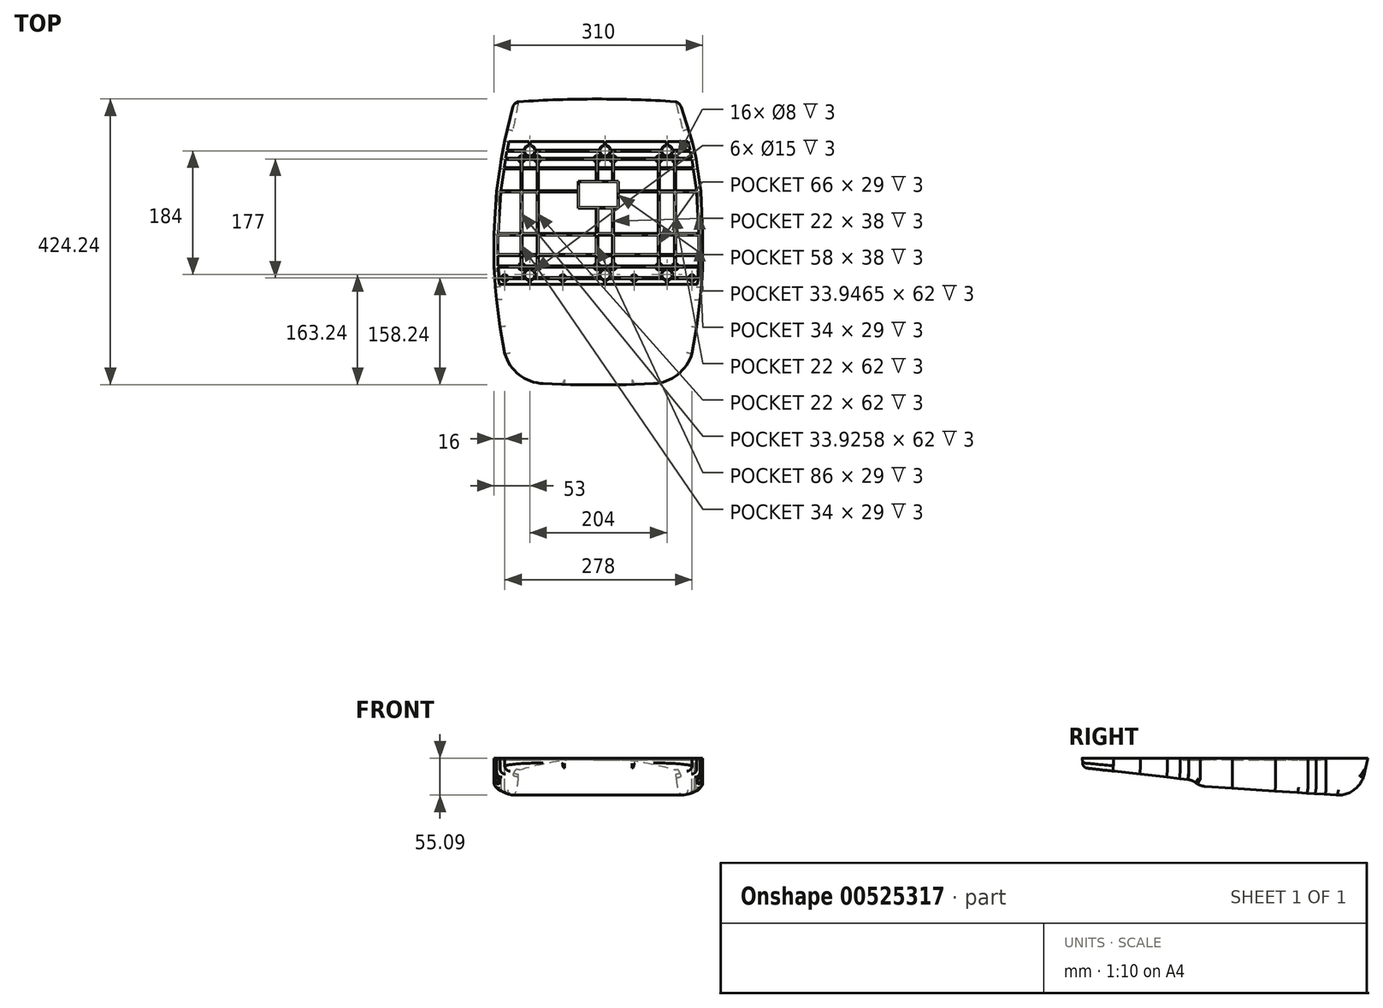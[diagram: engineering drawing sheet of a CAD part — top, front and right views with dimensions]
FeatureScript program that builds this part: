
annotation { "Feature Type Name" : "Feature", "Feature Type Description" : "" }
export const myFeature = defineFeature(function(context is Context, id is Id, definition is map)
    precondition{}
    {
        {
            var Q0;
            Q0=qCreatedBy(makeId("Top.planeOp"),FACE);
            var sketch = newSketch(context, id + "F0", { "sketchPlane" : qUnion([Q0])});
            skLineSegment(sketch, "E0.bottom", {"start": v(29, 19) * mm, "end": v(-29, 19) * mm});
            skLineSegment(sketch, "E0.top", {"start": v(29, -19) * mm, "end": v(-29, -19) * mm});
            skLineSegment(sketch, "E0.left", {"start": v(29, 19) * mm, "end": v(29, -19) * mm});
            skLineSegment(sketch, "E0.right", {"start": v(-29, 19) * mm, "end": v(-29, -19) * mm});
            skPoint(sketch, "E0.middle", {"position": v(0, 0) * mm});
            skLineSegment(sketch, "E1.0", {"start": v(30, 20) * mm, "end": v(-30, 20) * mm});
            skLineSegment(sketch, "E1.1", {"start": v(30, 20) * mm, "end": v(30, -20) * mm});
            skLineSegment(sketch, "E1.2", {"start": v(30, -20) * mm, "end": v(-30, -20) * mm});
            skLineSegment(sketch, "E1.3", {"start": v(-30, 20) * mm, "end": v(-30, -20) * mm});
            skLineSegment(sketch, "E2", {"start": v(-2, 53) * mm, "end": v(-2, -107) * mm, "construction": true});
            skLineSegment(sketch, "E3", {"start": v(22, 53) * mm, "end": v(22, -107) * mm, "construction": true});
            skLineSegment(sketch, "E4", {"start": v(-155, -107) * mm, "end": v(155, -107) * mm, "construction": true});
            skLineSegment(sketch, "E5", {"start": v(155, -90) * mm, "end": v(-155, -90) * mm, "construction": true});
            skLineSegment(sketch, "E6", {"start": v(-155, -59) * mm, "end": v(155, -59) * mm, "construction": true});
            skCircle(sketch, "E7", {"center": v(-2, -107) * mm, "radius": 5 * mm});
            skCircle(sketch, "E8", {"center": v(22, -107) * mm, "radius": 5 * mm});
            skLineSegment(sketch, "E9", {"start": v(154, -124) * mm, "end": v(-154, -124) * mm, "construction": true});
            skCircle(sketch, "E10", {"center": v(139, -124) * mm, "radius": 5 * mm});
            skCircle(sketch, "E11", {"center": v(53, -124) * mm, "radius": 5 * mm});
            skCircle(sketch, "E12", {"center": v(-53, -124) * mm, "radius": 5 * mm});
            skCircle(sketch, "E13", {"center": v(-139, -124) * mm, "radius": 5 * mm});
            skLineSegment(sketch, "E14", {"start": v(22, -107) * mm, "end": v(10, -119) * mm, "construction": true});
            skLineSegment(sketch, "E15", {"start": v(-2, -107) * mm, "end": v(10, -119) * mm, "construction": true});
            skCircle(sketch, "E16", {"center": v(10, -119) * mm, "radius": 8.5 * mm});
            skCircle(sketch, "E17", {"center": v(90, -107) * mm, "radius": 5 * mm});
            skCircle(sketch, "E18", {"center": v(114, -107) * mm, "radius": 5 * mm});
            skLineSegment(sketch, "E19", {"start": v(114, -107) * mm, "end": v(102, -119) * mm, "construction": true});
            skLineSegment(sketch, "E20", {"start": v(102, -119) * mm, "end": v(90, -107) * mm, "construction": true});
            skCircle(sketch, "E21", {"center": v(102, -119) * mm, "radius": 8.5 * mm});
            skCircle(sketch, "E22", {"center": v(-90, -107) * mm, "radius": 5 * mm});
            skCircle(sketch, "E23", {"center": v(-114, -107) * mm, "radius": 5 * mm});
            skLineSegment(sketch, "E24", {"start": v(-90, -107) * mm, "end": v(-102, -119) * mm, "construction": true});
            skLineSegment(sketch, "E25", {"start": v(-102, -119) * mm, "end": v(-114, -107) * mm, "construction": true});
            skCircle(sketch, "E26", {"center": v(-102, -119) * mm, "radius": 8.5 * mm});
            skLineSegment(sketch, "E27", {"start": v(-90, -107) * mm, "end": v(-90, 53) * mm, "construction": true});
            skLineSegment(sketch, "E28", {"start": v(-114, -107) * mm, "end": v(-114, 53) * mm, "construction": true});
            skLineSegment(sketch, "E29", {"start": v(114, -107) * mm, "end": v(114, 53) * mm, "construction": true});
            skLineSegment(sketch, "E30", {"start": v(145, 53) * mm, "end": v(-144, 53) * mm, "construction": true});
            skLineSegment(sketch, "E31", {"start": v(90, -107) * mm, "end": v(90, 53) * mm, "construction": true});
            skLineSegment(sketch, "E32", {"start": v(152, 5) * mm, "end": v(-151, 5) * mm, "construction": true});
            skLineSegment(sketch, "E33", {"start": v(142.5, 65) * mm, "end": v(-135.68, 65) * mm, "construction": true});
            skLineSegment(sketch, "E34", {"start": v(-146, 39) * mm, "end": v(147, 39) * mm, "construction": true});
            skCircle(sketch, "E35", {"center": v(-114, 53) * mm, "radius": 5 * mm});
            skCircle(sketch, "E36", {"center": v(-90, 53) * mm, "radius": 5 * mm});
            skCircle(sketch, "E37", {"center": v(-2, 53) * mm, "radius": 5 * mm});
            skCircle(sketch, "E38", {"center": v(22, 53) * mm, "radius": 5 * mm});
            skCircle(sketch, "E39", {"center": v(90, 53) * mm, "radius": 5 * mm});
            skCircle(sketch, "E40", {"center": v(114, 53) * mm, "radius": 5 * mm});
            skLineSegment(sketch, "E41", {"start": v(-114, 53) * mm, "end": v(-102, 65) * mm, "construction": true});
            skLineSegment(sketch, "E42", {"start": v(-102, 65) * mm, "end": v(-90, 53) * mm, "construction": true});
            skLineSegment(sketch, "E43", {"start": v(-2, 53) * mm, "end": v(10, 65) * mm, "construction": true});
            skLineSegment(sketch, "E44", {"start": v(10, 65) * mm, "end": v(22, 53) * mm, "construction": true});
            skLineSegment(sketch, "E45", {"start": v(90, 53) * mm, "end": v(102, 65) * mm, "construction": true});
            skLineSegment(sketch, "E46", {"start": v(102, 65) * mm, "end": v(114, 53) * mm, "construction": true});
            skCircle(sketch, "E47", {"center": v(102, 65) * mm, "radius": 8.5 * mm});
            skCircle(sketch, "E48", {"center": v(10, 65) * mm, "radius": 8.5 * mm});
            skCircle(sketch, "E49", {"center": v(-102, 65) * mm, "radius": 8.5 * mm});
            skLineSegment(sketch, "E50", {"start": v(-53, -133) * mm, "end": v(-53, -107) * mm, "construction": true});
            skLineSegment(sketch, "E51", {"start": v(10, -119) * mm, "end": v(10, -133) * mm, "construction": true});
            skLineSegment(sketch, "E52", {"start": v(53, -133) * mm, "end": v(53, -107) * mm, "construction": true});
            skLineSegment(sketch, "E53", {"start": v(139, -133) * mm, "end": v(139, -107) * mm, "construction": true});
            skLineSegment(sketch, "E54", {"start": v(102, -119) * mm, "end": v(102, -137) * mm, "construction": true});
            skLineSegment(sketch, "E55", {"start": v(-139, -133) * mm, "end": v(-139, -107) * mm, "construction": true});
            skLineSegment(sketch, "E56", {"start": v(-102, -119) * mm, "end": v(-102, -137) * mm, "construction": true});
            skLineSegment(sketch, "E57", {"start": v(-102, 65) * mm, "end": v(-102, 80) * mm, "construction": true});
            skLineSegment(sketch, "E58", {"start": v(10, 65) * mm, "end": v(10, 80) * mm, "construction": true});
            skLineSegment(sketch, "E59", {"start": v(102, 65) * mm, "end": v(102, 80) * mm, "construction": true});
            skLineSegment(sketch, "E60", {"start": v(23, -20) * mm, "end": v(23, -58) * mm});
            skLineSegment(sketch, "E61", {"start": v(23, -58) * mm, "end": v(89, -58) * mm});
            skLineSegment(sketch, "E62", {"start": v(89, -58) * mm, "end": v(89, 4) * mm});
            skLineSegment(sketch, "E63", {"start": v(89, 4) * mm, "end": v(30, 4) * mm});
            skLineSegment(sketch, "E64", {"start": v(21, -20) * mm, "end": v(21, -58) * mm});
            skLineSegment(sketch, "E65", {"start": v(21, -58) * mm, "end": v(-1, -58) * mm});
            skLineSegment(sketch, "E66", {"start": v(-1, -58) * mm, "end": v(-1, -20) * mm});
            skLineSegment(sketch, "E67", {"start": v(-3, -20) * mm, "end": v(-3, -58) * mm});
            skLineSegment(sketch, "E68", {"start": v(-3, -58) * mm, "end": v(-89, -58) * mm});
            skLineSegment(sketch, "E69", {"start": v(-89, -58) * mm, "end": v(-89, 4) * mm});
            skLineSegment(sketch, "E70", {"start": v(-89, 4) * mm, "end": v(-30, 4) * mm});
            skLineSegment(sketch, "E71", {"start": v(21, -60) * mm, "end": v(21, -89) * mm});
            skLineSegment(sketch, "E72", {"start": v(21, -89) * mm, "end": v(-1, -89) * mm});
            skLineSegment(sketch, "E73", {"start": v(-1, -89) * mm, "end": v(-1, -60) * mm});
            skLineSegment(sketch, "E74", {"start": v(-1, -60) * mm, "end": v(21, -60) * mm});
            skLineSegment(sketch, "E75", {"start": v(23, -60) * mm, "end": v(23, -89) * mm});
            skLineSegment(sketch, "E76", {"start": v(23, -89) * mm, "end": v(89, -89) * mm});
            skLineSegment(sketch, "E77", {"start": v(89, -89) * mm, "end": v(89, -60) * mm});
            skLineSegment(sketch, "E78", {"start": v(89, -60) * mm, "end": v(23, -60) * mm});
            skLineSegment(sketch, "E79", {"start": v(-3, -60) * mm, "end": v(-89, -60) * mm});
            skLineSegment(sketch, "E80", {"start": v(-89, -60) * mm, "end": v(-89, -89) * mm});
            skLineSegment(sketch, "E81", {"start": v(-89, -89) * mm, "end": v(-3, -89) * mm});
            skLineSegment(sketch, "E82", {"start": v(-3, -89) * mm, "end": v(-3, -60) * mm});
            skLineSegment(sketch, "E83", {"start": v(21, -91) * mm, "end": v(21, -102.1) * mm});
            skLineSegment(sketch, "E84", {"start": v(21, -91) * mm, "end": v(-1, -91) * mm});
            skLineSegment(sketch, "E85", {"start": v(-1, -91) * mm, "end": v(-1, -102.1) * mm});
            skLineSegment(sketch, "E86", {"start": v(2.9, -106) * mm, "end": v(17.1, -106) * mm});
            skLineSegment(sketch, "E87", {"start": v(17.83, -109.76) * mm, "end": v(15.26, -112.32) * mm});
            skLineSegment(sketch, "E88", {"start": v(4.74, -112.32) * mm, "end": v(2.17, -109.76) * mm});
            skLineSegment(sketch, "E89", {"start": v(2.9, -108) * mm, "end": v(17.1, -108) * mm});
            skLineSegment(sketch, "E90", {"start": v(19.24, -111.17) * mm, "end": v(16.68, -113.74) * mm});
            skLineSegment(sketch, "E91", {"start": v(0.76, -111.17) * mm, "end": v(3.32, -113.74) * mm});
            skCircle(sketch, "E92", {"center": v(10, -119) * mm, "radius": 7.5 * mm});
            skCircle(sketch, "E93", {"center": v(-2, -107) * mm, "radius": 4 * mm});
            skCircle(sketch, "E94", {"center": v(22, -107) * mm, "radius": 4 * mm});
            skCircle(sketch, "E95", {"center": v(53, -124) * mm, "radius": 4 * mm});
            skCircle(sketch, "E96", {"center": v(90, -107) * mm, "radius": 4 * mm});
            skCircle(sketch, "E97", {"center": v(114, -107) * mm, "radius": 4 * mm});
            skCircle(sketch, "E98", {"center": v(139, -124) * mm, "radius": 4 * mm});
            skCircle(sketch, "E99", {"center": v(-53, -124) * mm, "radius": 4 * mm});
            skCircle(sketch, "E100", {"center": v(-90, -107) * mm, "radius": 4 * mm});
            skCircle(sketch, "E101", {"center": v(-139, -124) * mm, "radius": 4 * mm});
            skCircle(sketch, "E102", {"center": v(-114, -107) * mm, "radius": 4 * mm});
            skCircle(sketch, "E103", {"center": v(-114, 53) * mm, "radius": 4 * mm});
            skCircle(sketch, "E104", {"center": v(-90, 53) * mm, "radius": 4 * mm});
            skCircle(sketch, "E105", {"center": v(-2, 53) * mm, "radius": 4 * mm});
            skCircle(sketch, "E106", {"center": v(114, 53) * mm, "radius": 4 * mm});
            skCircle(sketch, "E107", {"center": v(22, 53) * mm, "radius": 4 * mm});
            skCircle(sketch, "E108", {"center": v(90, 53) * mm, "radius": 4 * mm});
            skCircle(sketch, "E109", {"center": v(102, -119) * mm, "radius": 7.5 * mm});
            skCircle(sketch, "E110", {"center": v(-102, -119) * mm, "radius": 7.5 * mm});
            skCircle(sketch, "E111", {"center": v(-102, 65) * mm, "radius": 7.5 * mm});
            skCircle(sketch, "E112", {"center": v(10, 65) * mm, "radius": 7.5 * mm});
            skCircle(sketch, "E113", {"center": v(102, 65) * mm, "radius": 7.5 * mm});
            skLineSegment(sketch, "E114", {"start": v(17.5, -123) * mm, "end": v(48.1, -123) * mm});
            skLineSegment(sketch, "E115", {"start": v(48.1, -125) * mm, "end": v(16.02, -125) * mm});
            skLineSegment(sketch, "E116", {"start": v(26.9, -106) * mm, "end": v(85.1, -106) * mm});
            skLineSegment(sketch, "E117", {"start": v(23, -91) * mm, "end": v(23, -102.1) * mm});
            skLineSegment(sketch, "E118", {"start": v(23, -91) * mm, "end": v(89, -91) * mm});
            skLineSegment(sketch, "E119", {"start": v(89, -91) * mm, "end": v(89, -102.1) * mm});
            skLineSegment(sketch, "E120", {"start": v(26.9, -108) * mm, "end": v(85.1, -108) * mm});
            skLineSegment(sketch, "E121", {"start": v(57.9, -123) * mm, "end": v(94.5, -123) * mm});
            skLineSegment(sketch, "E122", {"start": v(95.32, -113.74) * mm, "end": v(92.76, -111.17) * mm});
            skLineSegment(sketch, "E123", {"start": v(96.74, -112.32) * mm, "end": v(94.17, -109.76) * mm});
            skLineSegment(sketch, "E124", {"start": v(94.9, -108) * mm, "end": v(109.1, -108) * mm});
            skLineSegment(sketch, "E125", {"start": v(107.26, -112.32) * mm, "end": v(109.83, -109.76) * mm});
            skLineSegment(sketch, "E126", {"start": v(108.68, -113.74) * mm, "end": v(111.24, -111.17) * mm});
            skLineSegment(sketch, "E127", {"start": v(109.5, -123) * mm, "end": v(134.1, -123) * mm});
            skLineSegment(sketch, "E128", {"start": v(118.9, -108) * mm, "end": v(148.93, -108) * mm});
            skLineSegment(sketch, "E129", {"start": v(91, -58) * mm, "end": v(113, -58) * mm});
            skLineSegment(sketch, "E130", {"start": v(113, -58) * mm, "end": v(113, 4) * mm});
            skLineSegment(sketch, "E131", {"start": v(113, 4) * mm, "end": v(91, 4) * mm});
            skLineSegment(sketch, "E132", {"start": v(91, 4) * mm, "end": v(91, -58) * mm});
            skLineSegment(sketch, "E133", {"start": v(91, -60) * mm, "end": v(91, -89) * mm});
            skLineSegment(sketch, "E134", {"start": v(91, -89) * mm, "end": v(113, -89) * mm});
            skLineSegment(sketch, "E135", {"start": v(113, -89) * mm, "end": v(113, -60) * mm});
            skLineSegment(sketch, "E136", {"start": v(113, -60) * mm, "end": v(91, -60) * mm});
            skLineSegment(sketch, "E137", {"start": v(91, -91) * mm, "end": v(91, -102.1) * mm});
            skLineSegment(sketch, "E138", {"start": v(91, -91) * mm, "end": v(113, -91) * mm});
            skLineSegment(sketch, "E139", {"start": v(113, -91) * mm, "end": v(113, -102.1) * mm});
            skLineSegment(sketch, "E140", {"start": v(89, 6) * mm, "end": v(30, 6) * mm});
            skLineSegment(sketch, "E141", {"start": v(89, 6) * mm, "end": v(89, 38) * mm});
            skLineSegment(sketch, "E142", {"start": v(89, 38) * mm, "end": v(23, 38) * mm});
            skLineSegment(sketch, "E143", {"start": v(23, 38) * mm, "end": v(23, 20) * mm});
            skLineSegment(sketch, "E144", {"start": v(91, 6) * mm, "end": v(113, 6) * mm});
            skLineSegment(sketch, "E145", {"start": v(113, 6) * mm, "end": v(113, 38) * mm});
            skLineSegment(sketch, "E146", {"start": v(113, 38) * mm, "end": v(91, 38) * mm});
            skLineSegment(sketch, "E147", {"start": v(91, 38) * mm, "end": v(91, 6) * mm});
            skLineSegment(sketch, "E148", {"start": v(113, 40) * mm, "end": v(113, 48.1) * mm});
            skLineSegment(sketch, "E149", {"start": v(113, 40) * mm, "end": v(91, 40) * mm});
            skLineSegment(sketch, "E150", {"start": v(91, 40) * mm, "end": v(91, 48.1) * mm});
            skLineSegment(sketch, "E151", {"start": v(94.9, 52) * mm, "end": v(109.1, 52) * mm});
            skLineSegment(sketch, "E152", {"start": v(89, 40) * mm, "end": v(89, 48.1) * mm});
            skLineSegment(sketch, "E153", {"start": v(89, 40) * mm, "end": v(23, 40) * mm});
            skLineSegment(sketch, "E154", {"start": v(23, 40) * mm, "end": v(23, 48.1) * mm});
            skLineSegment(sketch, "E155", {"start": v(85.1, 52) * mm, "end": v(26.9, 52) * mm});
            skLineSegment(sketch, "E156", {"start": v(21, 20) * mm, "end": v(21, 38) * mm});
            skLineSegment(sketch, "E157", {"start": v(21, 38) * mm, "end": v(-1, 38) * mm});
            skLineSegment(sketch, "E158", {"start": v(-1, 38) * mm, "end": v(-1, 20) * mm});
            skLineSegment(sketch, "E159", {"start": v(21, 40) * mm, "end": v(-1, 40) * mm});
            skLineSegment(sketch, "E160", {"start": v(-1, 40) * mm, "end": v(-1, 48.1) * mm});
            skLineSegment(sketch, "E161", {"start": v(17.1, 52) * mm, "end": v(2.9, 52) * mm});
            skLineSegment(sketch, "E162", {"start": v(21, 40) * mm, "end": v(21, 48.1) * mm});
            skLineSegment(sketch, "E163", {"start": v(-3, -91) * mm, "end": v(-89, -91) * mm});
            skLineSegment(sketch, "E164", {"start": v(-89, -91) * mm, "end": v(-89, -102.1) * mm});
            skLineSegment(sketch, "E165", {"start": v(-3, -91) * mm, "end": v(-3, -102.1) * mm});
            skLineSegment(sketch, "E166", {"start": v(-6.9, -106) * mm, "end": v(-85.1, -106) * mm});
            skLineSegment(sketch, "E167", {"start": v(-94.9, -106) * mm, "end": v(-109.1, -106) * mm});
            skLineSegment(sketch, "E168", {"start": v(-91, -58) * mm, "end": v(-113, -58) * mm});
            skLineSegment(sketch, "E169", {"start": v(-113, -58) * mm, "end": v(-113, 4) * mm});
            skLineSegment(sketch, "E170", {"start": v(-113, 4) * mm, "end": v(-91, 4) * mm});
            skLineSegment(sketch, "E171", {"start": v(-91, 4) * mm, "end": v(-91, -58) * mm});
            skLineSegment(sketch, "E172", {"start": v(-30, 6) * mm, "end": v(-89, 6) * mm});
            skLineSegment(sketch, "E173", {"start": v(-89, 6) * mm, "end": v(-89, 38) * mm});
            skLineSegment(sketch, "E174", {"start": v(-89, 38) * mm, "end": v(-3, 38) * mm});
            skLineSegment(sketch, "E175", {"start": v(-3, 38) * mm, "end": v(-3, 20) * mm});
            skLineSegment(sketch, "E176", {"start": v(-91, 6) * mm, "end": v(-113, 6) * mm});
            skLineSegment(sketch, "E177", {"start": v(-113, 6) * mm, "end": v(-113, 38) * mm});
            skLineSegment(sketch, "E178", {"start": v(-113, 38) * mm, "end": v(-91, 38) * mm});
            skLineSegment(sketch, "E179", {"start": v(-91, 38) * mm, "end": v(-91, 6) * mm});
            skLineSegment(sketch, "E180", {"start": v(-3, 40) * mm, "end": v(-89, 40) * mm});
            skLineSegment(sketch, "E181", {"start": v(-89, 40) * mm, "end": v(-89, 48.1) * mm});
            skLineSegment(sketch, "E182", {"start": v(-3, 40) * mm, "end": v(-3, 48.1) * mm});
            skLineSegment(sketch, "E183", {"start": v(-6.9, 52) * mm, "end": v(-85.1, 52) * mm});
            skLineSegment(sketch, "E184", {"start": v(-91, 40) * mm, "end": v(-113, 40) * mm});
            skLineSegment(sketch, "E185", {"start": v(-113, 40) * mm, "end": v(-113, 48.1) * mm});
            skLineSegment(sketch, "E186", {"start": v(-91, 40) * mm, "end": v(-91, 48.1) * mm});
            skLineSegment(sketch, "E187", {"start": v(-94.9, 52) * mm, "end": v(-109.1, 52) * mm});
            skLineSegment(sketch, "E188", {"start": v(57.9, -125) * mm, "end": v(95.98, -125) * mm});
            skLineSegment(sketch, "E189", {"start": v(108.02, -125) * mm, "end": v(134.1, -125) * mm});
            skLineSegment(sketch, "E190", {"start": v(3.98, -125) * mm, "end": v(-48.1, -125) * mm});
            skLineSegment(sketch, "E191", {"start": v(2.5, -123) * mm, "end": v(-48.1, -123) * mm});
            skLineSegment(sketch, "E192", {"start": v(-57.9, -125) * mm, "end": v(-95.98, -125) * mm});
            skLineSegment(sketch, "E193", {"start": v(-57.9, -123) * mm, "end": v(-94.5, -123) * mm});
            skLineSegment(sketch, "E194", {"start": v(-95.32, -113.74) * mm, "end": v(-92.76, -111.17) * mm});
            skLineSegment(sketch, "E195", {"start": v(-96.74, -112.32) * mm, "end": v(-94.17, -109.76) * mm});
            skLineSegment(sketch, "E196", {"start": v(-6.9, -108) * mm, "end": v(-85.1, -108) * mm});
            skLineSegment(sketch, "E197", {"start": v(-108.02, -125) * mm, "end": v(-134.1, -125) * mm});
            skLineSegment(sketch, "E198", {"start": v(-109.5, -123) * mm, "end": v(-134.1, -123) * mm});
            skLineSegment(sketch, "E199", {"start": v(-94.9, -108) * mm, "end": v(-109.1, -108) * mm});
            skLineSegment(sketch, "E200", {"start": v(-107.26, -112.32) * mm, "end": v(-109.83, -109.76) * mm});
            skLineSegment(sketch, "E201", {"start": v(-108.68, -113.74) * mm, "end": v(-111.24, -111.17) * mm});
            skLineSegment(sketch, "E202", {"start": v(2.9, 54) * mm, "end": v(17.1, 54) * mm});
            skLineSegment(sketch, "E203", {"start": v(26.9, 54) * mm, "end": v(85.1, 54) * mm});
            skLineSegment(sketch, "E204", {"start": v(94.9, 54) * mm, "end": v(109.1, 54) * mm});
            skLineSegment(sketch, "E205", {"start": v(109.83, 55.76) * mm, "end": v(107.26, 58.32) * mm});
            skLineSegment(sketch, "E206", {"start": v(111.24, 57.17) * mm, "end": v(108.68, 59.74) * mm});
            skLineSegment(sketch, "E207", {"start": v(96.74, 58.32) * mm, "end": v(94.17, 55.76) * mm});
            skLineSegment(sketch, "E208", {"start": v(92.76, 57.17) * mm, "end": v(95.32, 59.74) * mm});
            skLineSegment(sketch, "E209", {"start": v(93.56, 64) * mm, "end": v(18.44, 64) * mm});
            skLineSegment(sketch, "E210", {"start": v(93.56, 66) * mm, "end": v(18.44, 66) * mm});
            skLineSegment(sketch, "E211", {"start": v(19.24, 57.17) * mm, "end": v(16.68, 59.74) * mm});
            skLineSegment(sketch, "E212", {"start": v(17.83, 55.76) * mm, "end": v(15.26, 58.32) * mm});
            skLineSegment(sketch, "E213", {"start": v(2.17, 55.76) * mm, "end": v(4.74, 58.32) * mm});
            skLineSegment(sketch, "E214", {"start": v(0.76, 57.17) * mm, "end": v(3.32, 59.74) * mm});
            skLineSegment(sketch, "E215", {"start": v(-6.9, 54) * mm, "end": v(-85.1, 54) * mm});
            skLineSegment(sketch, "E216", {"start": v(-94.9, 54) * mm, "end": v(-109.1, 54) * mm});
            skLineSegment(sketch, "E217", {"start": v(-109.83, 55.76) * mm, "end": v(-107.26, 58.32) * mm});
            skLineSegment(sketch, "E218", {"start": v(-111.24, 57.17) * mm, "end": v(-108.68, 59.74) * mm});
            skLineSegment(sketch, "E219", {"start": v(-94.17, 55.76) * mm, "end": v(-96.74, 58.32) * mm});
            skLineSegment(sketch, "E220", {"start": v(-92.76, 57.17) * mm, "end": v(-95.32, 59.74) * mm});
            skLineSegment(sketch, "E221", {"start": v(1.56, 64) * mm, "end": v(-93.56, 64) * mm});
            skLineSegment(sketch, "E222", {"start": v(1.56, 66) * mm, "end": v(-93.56, 66) * mm});
            skLineSegment(sketch, "E223", {"start": v(-91, -60) * mm, "end": v(-113, -60) * mm});
            skLineSegment(sketch, "E224", {"start": v(-113, -60) * mm, "end": v(-113, -89) * mm});
            skLineSegment(sketch, "E225", {"start": v(-113, -89) * mm, "end": v(-91, -89) * mm});
            skLineSegment(sketch, "E226", {"start": v(-91, -89) * mm, "end": v(-91, -60) * mm});
            skLineSegment(sketch, "E227", {"start": v(-91, -91) * mm, "end": v(-113, -91) * mm});
            skLineSegment(sketch, "E228", {"start": v(-113, -91) * mm, "end": v(-113, -102.1) * mm});
            skLineSegment(sketch, "E229", {"start": v(-91, -91) * mm, "end": v(-91, -102.1) * mm});
            skLineSegment(sketch, "E230", {"start": v(-144, 53) * mm, "end": v(-146, 39) * mm});
            skLineSegment(sketch, "E231", {"start": v(-146, 39) * mm, "end": v(-151, 5) * mm});
            skLineSegment(sketch, "E232", {"start": v(-151, 5) * mm, "end": v(-155, -59) * mm});
            skLineSegment(sketch, "E233", {"start": v(-155, -59) * mm, "end": v(-155, -90) * mm});
            skLineSegment(sketch, "E234", {"start": v(-155, -90) * mm, "end": v(-155, -107) * mm});
            skLineSegment(sketch, "E235", {"start": v(-155, -107) * mm, "end": v(-154, -124) * mm});
            skLineSegment(sketch, "E236", {"start": v(142.5, 65) * mm, "end": v(145, 53) * mm});
            skLineSegment(sketch, "E237", {"start": v(145, 53) * mm, "end": v(147, 39) * mm});
            skLineSegment(sketch, "E238", {"start": v(147, 39) * mm, "end": v(152, 5) * mm});
            skLineSegment(sketch, "E239", {"start": v(152, 5) * mm, "end": v(155, -59) * mm});
            skLineSegment(sketch, "E240", {"start": v(155, -59) * mm, "end": v(155, -90) * mm});
            skLineSegment(sketch, "E241", {"start": v(155, -90) * mm, "end": v(155, -107) * mm});
            skLineSegment(sketch, "E242", {"start": v(155, -107) * mm, "end": v(154, -124) * mm});
            skLineSegment(sketch, "E243", {"start": v(139, 80) * mm, "end": v(-139, 80) * mm, "construction": true});
            skLineSegment(sketch, "E244", {"start": v(-139, 80) * mm, "end": v(-144, 53) * mm});
            skLineSegment(sketch, "E245", {"start": v(139, 80) * mm, "end": v(142.5, 65) * mm});
            skLineSegment(sketch, "E246", {"start": v(-153.3, -133) * mm, "end": v(153.3, -133) * mm, "construction": true});
            skLineSegment(sketch, "E247", {"start": v(-154, -124) * mm, "end": v(-153.3, -133) * mm});
            skLineSegment(sketch, "E248", {"start": v(154, -124) * mm, "end": v(153.3, -133) * mm});
            skLineSegment(sketch, "E249.0", {"start": v(148.01, -123.6) * mm, "end": v(147.29, -133) * mm});
            skLineSegment(sketch, "E249.1", {"start": v(149, -106.82) * mm, "end": v(148.01, -123.6) * mm});
            skLineSegment(sketch, "E249.2", {"start": v(149, -90) * mm, "end": v(149, -106.82) * mm});
            skLineSegment(sketch, "E249.3", {"start": v(149, -59.14) * mm, "end": v(149, -90) * mm});
            skLineSegment(sketch, "E249.4", {"start": v(146.02, 4.42) * mm, "end": v(149, -59.14) * mm});
            skLineSegment(sketch, "E249.5", {"start": v(133.07, 79) * mm, "end": v(136.64, 63.7) * mm});
            skLineSegment(sketch, "E249.6", {"start": v(136.64, 63.7) * mm, "end": v(139.09, 51.96) * mm});
            skLineSegment(sketch, "E249.7", {"start": v(139.09, 51.96) * mm, "end": v(141.06, 38.14) * mm});
            skLineSegment(sketch, "E249.8", {"start": v(141.06, 38.14) * mm, "end": v(146.02, 4.42) * mm});
            skLineSegment(sketch, "E250.0", {"start": v(-148.01, -123.6) * mm, "end": v(-147.29, -133) * mm});
            skLineSegment(sketch, "E250.1", {"start": v(-149, -106.82) * mm, "end": v(-148.01, -123.6) * mm});
            skLineSegment(sketch, "E250.2", {"start": v(-149, -90) * mm, "end": v(-149, -106.82) * mm});
            skLineSegment(sketch, "E250.3", {"start": v(-149, -59.19) * mm, "end": v(-149, -90) * mm});
            skLineSegment(sketch, "E250.4", {"start": v(-133.08, 79) * mm, "end": v(-138.08, 52.03) * mm});
            skLineSegment(sketch, "E250.5", {"start": v(-138.08, 52.03) * mm, "end": v(-140.06, 38.14) * mm});
            skLineSegment(sketch, "E250.6", {"start": v(-140.06, 38.14) * mm, "end": v(-145.03, 4.38) * mm});
            skLineSegment(sketch, "E250.7", {"start": v(-145.03, 4.38) * mm, "end": v(-149, -59.19) * mm});
            skLineSegment(sketch, "E251", {"start": v(147.29, -133) * mm, "end": v(-147.29, -133) * mm});
            skLineSegment(sketch, "E252", {"start": v(-133.08, 79) * mm, "end": v(133.07, 79) * mm});
            skLineSegment(sketch, "E253", {"start": v(-101, 79) * mm, "end": v(-101, 73.44) * mm});
            skLineSegment(sketch, "E254", {"start": v(-103, 79) * mm, "end": v(-103, 73.44) * mm});
            skLineSegment(sketch, "E255", {"start": v(-110.44, 66) * mm, "end": v(-135.5, 66) * mm});
            skLineSegment(sketch, "E256", {"start": v(-110.44, 64) * mm, "end": v(-135.86, 64) * mm});
            skLineSegment(sketch, "E257", {"start": v(-118.9, 54) * mm, "end": v(-137.71, 54) * mm});
            skLineSegment(sketch, "E258", {"start": v(-118.9, 52) * mm, "end": v(-138.08, 52.03) * mm});
            skLineSegment(sketch, "E259", {"start": v(118.9, 52) * mm, "end": v(139.09, 51.96) * mm});
            skLineSegment(sketch, "E260", {"start": v(118.9, 54) * mm, "end": v(138.66, 54) * mm});
            skLineSegment(sketch, "E261", {"start": v(110.44, 66) * mm, "end": v(136.1, 66) * mm});
            skLineSegment(sketch, "E262", {"start": v(110.44, 64) * mm, "end": v(136.57, 64) * mm});
            skLineSegment(sketch, "E263", {"start": v(101, 79) * mm, "end": v(101, 73.44) * mm});
            skLineSegment(sketch, "E264", {"start": v(103, 79) * mm, "end": v(103, 73.44) * mm});
            skLineSegment(sketch, "E265", {"start": v(11, 79) * mm, "end": v(11, 73.44) * mm});
            skLineSegment(sketch, "E266", {"start": v(9, 79) * mm, "end": v(9, 73.44) * mm});
            skLineSegment(sketch, "E267", {"start": v(115, -58) * mm, "end": v(115, 4) * mm});
            skLineSegment(sketch, "E268", {"start": v(115, -58) * mm, "end": v(148.95, -58) * mm});
            skLineSegment(sketch, "E269", {"start": v(115, 4) * mm, "end": v(146.04, 4) * mm});
            skLineSegment(sketch, "E270", {"start": v(115, 6) * mm, "end": v(115, 38) * mm});
            skLineSegment(sketch, "E271", {"start": v(115, 38) * mm, "end": v(141.08, 38) * mm});
            skLineSegment(sketch, "E272", {"start": v(115, 40) * mm, "end": v(115, 48.1) * mm});
            skLineSegment(sketch, "E273", {"start": v(115, 40) * mm, "end": v(140.8, 40) * mm});
            skLineSegment(sketch, "E274", {"start": v(115, 6) * mm, "end": v(145.79, 6) * mm});
            skLineSegment(sketch, "E275", {"start": v(115, -60) * mm, "end": v(115, -89) * mm});
            skLineSegment(sketch, "E276", {"start": v(115, -89) * mm, "end": v(149, -89) * mm});
            skLineSegment(sketch, "E277", {"start": v(115, -91) * mm, "end": v(115, -102.1) * mm});
            skLineSegment(sketch, "E278", {"start": v(115, -91) * mm, "end": v(149, -91) * mm});
            skLineSegment(sketch, "E279", {"start": v(94.9, -106) * mm, "end": v(109.1, -106) * mm});
            skLineSegment(sketch, "E280", {"start": v(118.9, -106) * mm, "end": v(149, -106) * mm});
            skLineSegment(sketch, "E281", {"start": v(115, -60) * mm, "end": v(149, -60) * mm});
            skLineSegment(sketch, "E282", {"start": v(143.9, -123) * mm, "end": v(148.05, -123) * mm});
            skLineSegment(sketch, "E283", {"start": v(143.9, -125) * mm, "end": v(147.9, -125) * mm});
            skLineSegment(sketch, "E284", {"start": v(103, -133) * mm, "end": v(103, -127.44) * mm});
            skLineSegment(sketch, "E285", {"start": v(101, -133) * mm, "end": v(101, -127.44) * mm});
            skLineSegment(sketch, "E286", {"start": v(11, -133) * mm, "end": v(11, -127.44) * mm});
            skLineSegment(sketch, "E287", {"start": v(9, -133) * mm, "end": v(9, -127.44) * mm});
            skLineSegment(sketch, "E288", {"start": v(-101, -133) * mm, "end": v(-101, -127.44) * mm});
            skLineSegment(sketch, "E289", {"start": v(-103, -133) * mm, "end": v(-103, -127.44) * mm});
            skLineSegment(sketch, "E290", {"start": v(-143.9, -123) * mm, "end": v(-148.05, -123) * mm});
            skLineSegment(sketch, "E291", {"start": v(-143.9, -125) * mm, "end": v(-147.9, -125) * mm});
            skLineSegment(sketch, "E292", {"start": v(-118.9, -106) * mm, "end": v(-149, -106) * mm});
            skLineSegment(sketch, "E293", {"start": v(-118.9, -108) * mm, "end": v(-148.93, -108) * mm});
            skLineSegment(sketch, "E294", {"start": v(-115, -58) * mm, "end": v(-115, 4) * mm});
            skLineSegment(sketch, "E295", {"start": v(-115, 4) * mm, "end": v(-145.05, 4) * mm});
            skLineSegment(sketch, "E296", {"start": v(-115, -58) * mm, "end": v(-148.93, -58) * mm});
            skLineSegment(sketch, "E297", {"start": v(-115, -60) * mm, "end": v(-149, -60) * mm});
            skLineSegment(sketch, "E298", {"start": v(-115, -60) * mm, "end": v(-115, -89) * mm});
            skLineSegment(sketch, "E299", {"start": v(-115, -89) * mm, "end": v(-149, -89) * mm});
            skLineSegment(sketch, "E300", {"start": v(-115, -91) * mm, "end": v(-149, -91) * mm});
            skLineSegment(sketch, "E301", {"start": v(-115, -91) * mm, "end": v(-115, -102.1) * mm});
            skLineSegment(sketch, "E302", {"start": v(-115, 6) * mm, "end": v(-144.79, 6) * mm});
            skLineSegment(sketch, "E303", {"start": v(-115, 6) * mm, "end": v(-115, 38) * mm});
            skLineSegment(sketch, "E304", {"start": v(-115, 38) * mm, "end": v(-140.08, 38) * mm});
            skLineSegment(sketch, "E305", {"start": v(-115, 40) * mm, "end": v(-139.8, 40) * mm});
            skLineSegment(sketch, "E306", {"start": v(-115, 40) * mm, "end": v(-115, 48.1) * mm});
            skLineSegment(sketch, "E307", {"start": v(-153, -137) * mm, "end": v(153, -137) * mm});
            skLineSegment(sketch, "E308", {"start": v(153.3, -133) * mm, "end": v(153, -137) * mm});
            skLineSegment(sketch, "E309", {"start": v(-153.3, -133) * mm, "end": v(-153, -137) * mm});
            skLineSegment(sketch, "E310", {"start": v(-127, 130) * mm, "end": v(123, 130) * mm, "construction": true});
            skLineSegment(sketch, "E311", {"start": v(139, 80) * mm, "end": v(123, 130) * mm});
            skLineSegment(sketch, "E312", {"start": v(-139, 80) * mm, "end": v(-127, 130) * mm});
            skLineSegment(sketch, "E313", {"start": v(-119.5, 138) * mm, "end": v(115.5, 138) * mm, "construction": true});
            skLineSegment(sketch, "E314", {"start": v(-2, 53) * mm, "end": v(-2, 130) * mm, "construction": true});
            skLineSegment(sketch, "E315", {"start": v(-2, 130) * mm, "end": v(-2, 138) * mm, "construction": true});
            skLineSegment(sketch, "E316", {"start": v(-2, 138) * mm, "end": v(-2, 142) * mm, "construction": true});
            skArc(sketch, "E317", {"start": v(-127, 130) * mm, "mid": v(-124.3, 135) * mm, "end": v(-119.5, 138) * mm});
            skArc(sketch, "E318", {"start": v(123, 130) * mm, "mid": v(120.15, 134.85) * mm, "end": v(115.5, 138) * mm});
            skArc(sketch, "E319", {"start": v(115.5, 138) * mm, "mid": v(-2, 142) * mm, "end": v(-119.5, 138) * mm});
            skSolve(sketch);
        }
        {
            var Q0;
            Q0=qCreatedBy(makeId("Top.planeOp"),FACE);
            var sketch = newSketch(context, id + "F1", { "sketchPlane" : qUnion([Q0])});
            skLineSegment(sketch, "E320.0", {"start": v(-153, -137) * mm, "end": v(153, -137) * mm});
            skLineSegment(sketch, "E321", {"start": v(0, -137) * mm, "end": v(0, -282.5) * mm, "construction": true});
            skPoint(sketch, "E321.endSnap0", {"position": v(0, -137) * mm});
            skLineSegment(sketch, "E322", {"start": v(0, -156) * mm, "end": v(-151, -156) * mm, "construction": true});
            skLineSegment(sketch, "E323", {"start": v(0, -196) * mm, "end": v(-146, -196) * mm, "construction": true});
            skLineSegment(sketch, "E324", {"start": v(0, -236) * mm, "end": v(-139, -236) * mm, "construction": true});
            skLineSegment(sketch, "E325", {"start": v(-153, -137) * mm, "end": v(-151, -156) * mm});
            skLineSegment(sketch, "E326", {"start": v(-151, -156) * mm, "end": v(-146, -196) * mm});
            skLineSegment(sketch, "E327", {"start": v(-146, -196) * mm, "end": v(-139, -236) * mm});
            skCircle(sketch, "E328", {"center": v(0, -156) * mm, "radius": 9.5 * mm});
            skCircle(sketch, "E329", {"center": v(0, -156) * mm, "radius": 7.5 * mm});
            skCircle(sketch, "E330", {"center": v(0, -196) * mm, "radius": 9.5 * mm});
            skCircle(sketch, "E331", {"center": v(0, -196) * mm, "radius": 7.5 * mm});
            skCircle(sketch, "E332", {"center": v(0, -236) * mm, "radius": 9.5 * mm});
            skCircle(sketch, "E333", {"center": v(0, -236) * mm, "radius": 7.5 * mm});
            skLineSegment(sketch, "E334", {"start": v(-56, -137) * mm, "end": v(-40.71, -282.24) * mm, "construction": true});
            skLineSegment(sketch, "E335", {"start": v(-112, -137) * mm, "end": v(-81.73, -280.77) * mm, "construction": true});
            skCircle(sketch, "E336", {"center": v(-45.58, -236) * mm, "radius": 9.5 * mm});
            skCircle(sketch, "E337", {"center": v(-91.93, -232.33) * mm, "radius": 9.5 * mm});
            skCircle(sketch, "E338", {"center": v(-99.97, -194.16) * mm, "radius": 9.5 * mm});
            skCircle(sketch, "E339", {"center": v(-49.79, -196) * mm, "radius": 9.5 * mm});
            skCircle(sketch, "E340", {"center": v(-108, -156) * mm, "radius": 9.5 * mm});
            skCircle(sketch, "E341", {"center": v(-54, -156) * mm, "radius": 9.5 * mm});
            skCircle(sketch, "E342", {"center": v(-54, -156) * mm, "radius": 7.5 * mm});
            skCircle(sketch, "E343", {"center": v(-108, -156) * mm, "radius": 7.5 * mm});
            skCircle(sketch, "E344", {"center": v(-99.97, -194.16) * mm, "radius": 7.5 * mm});
            skCircle(sketch, "E345", {"center": v(-49.79, -196) * mm, "radius": 7.5 * mm});
            skCircle(sketch, "E346", {"center": v(-91.93, -232.33) * mm, "radius": 7.5 * mm});
            skCircle(sketch, "E347", {"center": v(-45.58, -236) * mm, "radius": 7.5 * mm});
            skLineSegment(sketch, "E348", {"start": v(-81.73, -280.77) * mm, "end": v(-40.71, -282.24) * mm});
            skLineSegment(sketch, "E349", {"start": v(0, -282.5) * mm, "end": v(-40.71, -282.24) * mm});
            skArc(sketch, "E350", {"start": v(-81.73, -280.77) * mm, "mid": v(-117.63, -267.67) * mm, "end": v(-139, -236) * mm});
            skCircle(sketch, "E351.MirrorC", {"center": v(54, -156) * mm, "radius": 7.5 * mm});
            skCircle(sketch, "E352.MirrorC", {"center": v(54, -156) * mm, "radius": 9.5 * mm});
            skCircle(sketch, "E353.MirrorC", {"center": v(49.79, -196) * mm, "radius": 7.5 * mm});
            skCircle(sketch, "E354.MirrorC", {"center": v(49.79, -196) * mm, "radius": 9.5 * mm});
            skCircle(sketch, "E355.MirrorC", {"center": v(45.58, -236) * mm, "radius": 7.5 * mm});
            skCircle(sketch, "E356.MirrorC", {"center": v(45.58, -236) * mm, "radius": 9.5 * mm});
            skCircle(sketch, "E357.MirrorC", {"center": v(91.93, -232.33) * mm, "radius": 7.5 * mm});
            skCircle(sketch, "E358.MirrorC", {"center": v(91.93, -232.33) * mm, "radius": 9.5 * mm});
            skCircle(sketch, "E359.MirrorC", {"center": v(99.97, -194.16) * mm, "radius": 7.5 * mm});
            skCircle(sketch, "E360.MirrorC", {"center": v(99.97, -194.16) * mm, "radius": 9.5 * mm});
            skCircle(sketch, "E361.MirrorC", {"center": v(108, -156) * mm, "radius": 7.5 * mm});
            skCircle(sketch, "E362.MirrorC", {"center": v(108, -156) * mm, "radius": 9.5 * mm});
            skLineSegment(sketch, "E363.MirrorCS", {"start": v(153, -137) * mm, "end": v(151, -156) * mm});
            skLineSegment(sketch, "E364.MirrorCS", {"start": v(151, -156) * mm, "end": v(146, -196) * mm});
            skLineSegment(sketch, "E365.MirrorCS", {"start": v(146, -196) * mm, "end": v(139, -236) * mm});
            skArc(sketch, "E366.MirrorCS", {"start": v(81.73, -280.77) * mm, "mid": v(117.63, -267.67) * mm, "end": v(139, -236) * mm});
            skLineSegment(sketch, "E367.MirrorCS", {"start": v(81.73, -280.77) * mm, "end": v(40.71, -282.24) * mm});
            skLineSegment(sketch, "E368.MirrorCS", {"start": v(0, -282.5) * mm, "end": v(40.71, -282.24) * mm});
            skSolve(sketch);
        }
        {
            var Q0;
            Q0=qCreatedBy(makeId("Top.planeOp"),FACE);
            var sketch = newSketch(context, id + "F2", { "sketchPlane" : qUnion([Q0])});
            skLineSegment(sketch, "E369.0", {"start": v(0, -282.5) * mm, "end": v(-40.71, -282.24) * mm});
            skLineSegment(sketch, "E370.0", {"start": v(-81.73, -280.77) * mm, "end": v(-40.71, -282.24) * mm});
            skArc(sketch, "E371.0", {"start": v(-81.73, -280.77) * mm, "mid": v(-117.63, -267.67) * mm, "end": v(-139, -236) * mm});
            skLineSegment(sketch, "E372.0", {"start": v(-146, -196) * mm, "end": v(-139, -236) * mm});
            skLineSegment(sketch, "E373.0", {"start": v(-151, -156) * mm, "end": v(-146, -196) * mm});
            skLineSegment(sketch, "E374.0", {"start": v(-153, -137) * mm, "end": v(-151, -156) * mm});
            skLineSegment(sketch, "E375.0", {"start": v(-153.3, -133) * mm, "end": v(-153, -137) * mm});
            skLineSegment(sketch, "E376.0", {"start": v(-154, -124) * mm, "end": v(-153.3, -133) * mm});
            skLineSegment(sketch, "E377.0", {"start": v(-155, -107) * mm, "end": v(-154, -124) * mm});
            skLineSegment(sketch, "E378.0", {"start": v(-155, -90) * mm, "end": v(-155, -107) * mm});
            skLineSegment(sketch, "E379.0", {"start": v(-155, -59) * mm, "end": v(-155, -90) * mm});
            skLineSegment(sketch, "E380.0", {"start": v(-151, 5) * mm, "end": v(-155, -59) * mm});
            skLineSegment(sketch, "E381.0", {"start": v(-146, 39) * mm, "end": v(-151, 5) * mm});
            skLineSegment(sketch, "E382.0", {"start": v(-144, 53) * mm, "end": v(-146, 39) * mm});
            skLineSegment(sketch, "E383.0", {"start": v(-139, 80) * mm, "end": v(-144, 53) * mm});
            skLineSegment(sketch, "E384.0", {"start": v(-139, 80) * mm, "end": v(-127, 130) * mm});
            skArc(sketch, "E385.0", {"start": v(-127, 130) * mm, "mid": v(-124.3, 135) * mm, "end": v(-119.5, 138) * mm});
            skArc(sketch, "E386.0", {"start": v(123, 130) * mm, "mid": v(120.15, 134.85) * mm, "end": v(115.5, 138) * mm});
            skLineSegment(sketch, "E387.0", {"start": v(139, 80) * mm, "end": v(123, 130) * mm});
            skLineSegment(sketch, "E388.0", {"start": v(139, 80) * mm, "end": v(142.5, 65) * mm});
            skLineSegment(sketch, "E389.0", {"start": v(142.5, 65) * mm, "end": v(145, 53) * mm});
            skLineSegment(sketch, "E390.0", {"start": v(145, 53) * mm, "end": v(147, 39) * mm});
            skLineSegment(sketch, "E391.0", {"start": v(147, 39) * mm, "end": v(152, 5) * mm});
            skLineSegment(sketch, "E392.0", {"start": v(152, 5) * mm, "end": v(155, -59) * mm});
            skLineSegment(sketch, "E393.0", {"start": v(155, -59) * mm, "end": v(155, -90) * mm});
            skLineSegment(sketch, "E394.0", {"start": v(155, -90) * mm, "end": v(155, -107) * mm});
            skLineSegment(sketch, "E395.0", {"start": v(155, -107) * mm, "end": v(154, -124) * mm});
            skLineSegment(sketch, "E396.0", {"start": v(154, -124) * mm, "end": v(153.3, -133) * mm});
            skLineSegment(sketch, "E397.0", {"start": v(153.3, -133) * mm, "end": v(153, -137) * mm});
            skLineSegment(sketch, "E398.0", {"start": v(153, -137) * mm, "end": v(151, -156) * mm});
            skLineSegment(sketch, "E399.0", {"start": v(151, -156) * mm, "end": v(146, -196) * mm});
            skLineSegment(sketch, "E400.0", {"start": v(146, -196) * mm, "end": v(139, -236) * mm});
            skArc(sketch, "E401.0", {"start": v(81.73, -280.77) * mm, "mid": v(117.63, -267.67) * mm, "end": v(139, -236) * mm});
            skLineSegment(sketch, "E402.0", {"start": v(81.73, -280.77) * mm, "end": v(40.71, -282.24) * mm});
            skLineSegment(sketch, "E403.0", {"start": v(0, -282.5) * mm, "end": v(40.71, -282.24) * mm});
            skArc(sketch, "E404.0", {"start": v(115.5, 138) * mm, "mid": v(-2, 142) * mm, "end": v(-119.5, 138) * mm});
            skSolve(sketch);
        }
        {
            var Q0;
            Q0=makeQuery(id+"F2.imprint","IMPRINT",FACE,{"disambiguationData":[TD([[makeQuery(id+"F2.imprint","IMPRINT",EDGE,{"derivedFrom":sQuery(id+"F2.wireOp",EDGE,"E369.0")}),-1.0]])]});
            extrude(context, id + "F3", {"entities" : qUnion([Q0]), "oppositeDirection" : true, "depth" : 60 * mm, "offsetDistance" : 25 * mm});
        }
        {
            var Q0;
            Q0=makeQuery(id+"F0.imprint","IMPRINT",FACE,{"disambiguationData":[TD([[makeQuery(id+"F0.imprint","IMPRINT",EDGE,{"derivedFrom":sQuery(id+"F0.wireOp",EDGE,"E110")}),1.0]])]});
            var Q1;
            Q1=makeQuery(id+"F0.imprint","IMPRINT",FACE,{"disambiguationData":[TD([[makeQuery(id+"F0.imprint","IMPRINT",EDGE,{"derivedFrom":sQuery(id+"F0.wireOp",EDGE,"E92")}),1.0]])]});
            var Q2;
            Q2=makeQuery(id+"F0.imprint","IMPRINT",FACE,{"disambiguationData":[TD([[makeQuery(id+"F0.imprint","IMPRINT",EDGE,{"derivedFrom":sQuery(id+"F0.wireOp",EDGE,"E101")}),1.0]])]});
            var Q3;
            Q3=makeQuery(id+"F0.imprint","IMPRINT",FACE,{"disambiguationData":[TD([[makeQuery(id+"F0.imprint","IMPRINT",EDGE,{"derivedFrom":sQuery(id+"F0.wireOp",EDGE,"E102")}),1.0]])]});
            var Q4;
            Q4=makeQuery(id+"F0.imprint","IMPRINT",FACE,{"disambiguationData":[TD([[makeQuery(id+"F0.imprint","IMPRINT",EDGE,{"derivedFrom":sQuery(id+"F0.wireOp",EDGE,"E100")}),1.0]])]});
            var Q5;
            Q5=makeQuery(id+"F0.imprint","IMPRINT",FACE,{"disambiguationData":[TD([[makeQuery(id+"F0.imprint","IMPRINT",EDGE,{"derivedFrom":sQuery(id+"F0.wireOp",EDGE,"E99")}),1.0]])]});
            var Q6;
            Q6=makeQuery(id+"F0.imprint","IMPRINT",FACE,{"disambiguationData":[TD([[makeQuery(id+"F0.imprint","IMPRINT",EDGE,{"derivedFrom":sQuery(id+"F0.wireOp",EDGE,"E93")}),1.0]])]});
            var Q7;
            Q7=makeQuery(id+"F0.imprint","IMPRINT",FACE,{"disambiguationData":[TD([[makeQuery(id+"F0.imprint","IMPRINT",EDGE,{"derivedFrom":sQuery(id+"F0.wireOp",EDGE,"E94")}),1.0]])]});
            var Q8;
            Q8=makeQuery(id+"F0.imprint","IMPRINT",FACE,{"disambiguationData":[TD([[makeQuery(id+"F0.imprint","IMPRINT",EDGE,{"derivedFrom":sQuery(id+"F0.wireOp",EDGE,"E95")}),1.0]])]});
            var Q9;
            Q9=makeQuery(id+"F0.imprint","IMPRINT",FACE,{"disambiguationData":[TD([[makeQuery(id+"F0.imprint","IMPRINT",EDGE,{"derivedFrom":sQuery(id+"F0.wireOp",EDGE,"E98")}),1.0]])]});
            var Q10;
            Q10=makeQuery(id+"F0.imprint","IMPRINT",FACE,{"disambiguationData":[TD([[makeQuery(id+"F0.imprint","IMPRINT",EDGE,{"derivedFrom":sQuery(id+"F0.wireOp",EDGE,"E109")}),1.0]])]});
            var Q11;
            Q11=makeQuery(id+"F0.imprint","IMPRINT",FACE,{"disambiguationData":[TD([[makeQuery(id+"F0.imprint","IMPRINT",EDGE,{"derivedFrom":sQuery(id+"F0.wireOp",EDGE,"E97")}),1.0]])]});
            var Q12;
            Q12=makeQuery(id+"F0.imprint","IMPRINT",FACE,{"disambiguationData":[TD([[makeQuery(id+"F0.imprint","IMPRINT",EDGE,{"derivedFrom":sQuery(id+"F0.wireOp",EDGE,"E96")}),1.0]])]});
            var Q13;
            Q13=makeQuery(id+"F0.imprint","IMPRINT",FACE,{"disambiguationData":[TD([[makeQuery(id+"F0.imprint","IMPRINT",EDGE,{"derivedFrom":sQuery(id+"F0.wireOp",EDGE,"E106")}),1.0]])]});
            var Q14;
            Q14=makeQuery(id+"F0.imprint","IMPRINT",FACE,{"disambiguationData":[TD([[makeQuery(id+"F0.imprint","IMPRINT",EDGE,{"derivedFrom":sQuery(id+"F0.wireOp",EDGE,"E108")}),1.0]])]});
            var Q15;
            Q15=makeQuery(id+"F0.imprint","IMPRINT",FACE,{"disambiguationData":[TD([[makeQuery(id+"F0.imprint","IMPRINT",EDGE,{"derivedFrom":sQuery(id+"F0.wireOp",EDGE,"E113")}),1.0]])]});
            var Q16;
            Q16=makeQuery(id+"F0.imprint","IMPRINT",FACE,{"disambiguationData":[TD([[makeQuery(id+"F0.imprint","IMPRINT",EDGE,{"derivedFrom":sQuery(id+"F0.wireOp",EDGE,"E107")}),1.0]])]});
            var Q17;
            Q17=makeQuery(id+"F0.imprint","IMPRINT",FACE,{"disambiguationData":[TD([[makeQuery(id+"F0.imprint","IMPRINT",EDGE,{"derivedFrom":sQuery(id+"F0.wireOp",EDGE,"E112")}),1.0]])]});
            var Q18;
            Q18=makeQuery(id+"F0.imprint","IMPRINT",FACE,{"disambiguationData":[TD([[makeQuery(id+"F0.imprint","IMPRINT",EDGE,{"derivedFrom":sQuery(id+"F0.wireOp",EDGE,"E105")}),1.0]])]});
            var Q19;
            Q19=makeQuery(id+"F0.imprint","IMPRINT",FACE,{"disambiguationData":[TD([[makeQuery(id+"F0.imprint","IMPRINT",EDGE,{"derivedFrom":sQuery(id+"F0.wireOp",EDGE,"E103")}),1.0]])]});
            var Q20;
            Q20=makeQuery(id+"F0.imprint","IMPRINT",FACE,{"disambiguationData":[TD([[makeQuery(id+"F0.imprint","IMPRINT",EDGE,{"derivedFrom":sQuery(id+"F0.wireOp",EDGE,"E104")}),1.0]])]});
            var Q21;
            Q21=makeQuery(id+"F0.imprint","IMPRINT",FACE,{"disambiguationData":[TD([[makeQuery(id+"F0.imprint","IMPRINT",EDGE,{"derivedFrom":sQuery(id+"F0.wireOp",EDGE,"E111")}),1.0]])]});
            extrude(context, id + "F4", {"entities" : qUnion([Q0, Q1, Q2, Q3, Q4, Q5, Q6, Q7, Q8, Q9, Q10, Q11, Q12, Q13, Q14, Q15, Q16, Q17, Q18, Q19, Q20, Q21]), "operationType" : NewBodyOperationType.REMOVE, "oppositeDirection" : true, "depth" : 3 * mm, "offsetDistance" : 25 * mm});
        }
        {
            var Q0;
            {var subQ4=sQuery(id+"F0.wireOp",EDGE,"E261");Q0=makeQuery(id+"F0.imprint","IMPRINT",FACE,{"disambiguationData":[TD([[makeQuery(id+"F0.imprint","IMPRINT",EDGE,{"derivedFrom":subQ4}),1.0]])]});}
            var Q1;
            {var subQ0=sQuery(id+"F0.wireOp",EDGE,"E206");Q1=makeQuery(id+"F0.imprint","IMPRINT",FACE,{"disambiguationData":[TD([[makeQuery(id+"F0.imprint","IMPRINT",EDGE,{"derivedFrom":subQ0}),-1.0]])]});}
            var Q2;
            {var subQ1=sQuery(id+"F0.wireOp",EDGE,"E259");Q2=makeQuery(id+"F0.imprint","IMPRINT",FACE,{"disambiguationData":[TD([[makeQuery(id+"F0.imprint","IMPRINT",EDGE,{"derivedFrom":subQ1}),-1.0]])]});}
            var Q3;
            Q3=makeQuery(id+"F0.imprint","IMPRINT",FACE,{"disambiguationData":[TD([[makeQuery(id+"F0.imprint","IMPRINT",EDGE,{"derivedFrom":sQuery(id+"F0.wireOp",EDGE,"E270")}),-1.0]])]});
            var Q4;
            Q4=makeQuery(id+"F0.imprint","IMPRINT",FACE,{"disambiguationData":[TD([[makeQuery(id+"F0.imprint","IMPRINT",EDGE,{"derivedFrom":sQuery(id+"F0.wireOp",EDGE,"E267")}),-1.0]])]});
            var Q5;
            Q5=makeQuery(id+"F0.imprint","IMPRINT",FACE,{"disambiguationData":[TD([[makeQuery(id+"F0.imprint","IMPRINT",EDGE,{"derivedFrom":sQuery(id+"F0.wireOp",EDGE,"E275")}),1.0]])]});
            var Q6;
            {var subQ0=sQuery(id+"F0.wireOp",EDGE,"E277");Q6=makeQuery(id+"F0.imprint","IMPRINT",FACE,{"disambiguationData":[TD([[makeQuery(id+"F0.imprint","IMPRINT",EDGE,{"derivedFrom":subQ0}),1.0]])]});}
            var Q7;
            {var subQ0=sQuery(id+"F0.wireOp",EDGE,"E126");Q7=makeQuery(id+"F0.imprint","IMPRINT",FACE,{"disambiguationData":[TD([[makeQuery(id+"F0.imprint","IMPRINT",EDGE,{"derivedFrom":subQ0}),-1.0]])]});}
            var Q8;
            {var subQ0=sQuery(id+"F0.wireOp",EDGE,"E189");Q8=makeQuery(id+"F0.imprint","IMPRINT",FACE,{"disambiguationData":[TD([[makeQuery(id+"F0.imprint","IMPRINT",EDGE,{"derivedFrom":subQ0}),-1.0]])]});}
            var Q9;
            {var subQ0=sQuery(id+"F0.wireOp",EDGE,"E123");Q9=makeQuery(id+"F0.imprint","IMPRINT",FACE,{"disambiguationData":[TD([[makeQuery(id+"F0.imprint","IMPRINT",EDGE,{"derivedFrom":subQ0}),-1.0]])]});}
            var Q10;
            {var subQ3=sQuery(id+"F0.wireOp",EDGE,"E115");Q10=makeQuery(id+"F0.imprint","IMPRINT",FACE,{"disambiguationData":[TD([[makeQuery(id+"F0.imprint","IMPRINT",EDGE,{"derivedFrom":subQ3}),1.0]])]});}
            var Q11;
            {var subQ4=sQuery(id+"F0.wireOp",EDGE,"E90");Q11=makeQuery(id+"F0.imprint","IMPRINT",FACE,{"disambiguationData":[TD([[makeQuery(id+"F0.imprint","IMPRINT",EDGE,{"derivedFrom":subQ4}),1.0]])]});}
            var Q12;
            {var subQ3=sQuery(id+"F0.wireOp",EDGE,"E137");Q12=makeQuery(id+"F0.imprint","IMPRINT",FACE,{"disambiguationData":[TD([[makeQuery(id+"F0.imprint","IMPRINT",EDGE,{"derivedFrom":subQ3}),1.0]])]});}
            var Q13;
            Q13=makeQuery(id+"F0.imprint","IMPRINT",FACE,{"disambiguationData":[TD([[makeQuery(id+"F0.imprint","IMPRINT",EDGE,{"derivedFrom":sQuery(id+"F0.wireOp",EDGE,"E133")}),1.0]])]});
            var Q14;
            Q14=makeQuery(id+"F0.imprint","IMPRINT",FACE,{"disambiguationData":[TD([[makeQuery(id+"F0.imprint","IMPRINT",EDGE,{"derivedFrom":sQuery(id+"F0.wireOp",EDGE,"E129")}),1.0]])]});
            var Q15;
            Q15=makeQuery(id+"F0.imprint","IMPRINT",FACE,{"disambiguationData":[TD([[makeQuery(id+"F0.imprint","IMPRINT",EDGE,{"derivedFrom":sQuery(id+"F0.wireOp",EDGE,"E144")}),1.0]])]});
            var Q16;
            {var subQ0=sQuery(id+"F0.wireOp",EDGE,"E148");Q16=makeQuery(id+"F0.imprint","IMPRINT",FACE,{"disambiguationData":[TD([[makeQuery(id+"F0.imprint","IMPRINT",EDGE,{"derivedFrom":subQ0}),1.0]])]});}
            var Q17;
            {var subQ3=sQuery(id+"F0.wireOp",EDGE,"E204");Q17=makeQuery(id+"F0.imprint","IMPRINT",FACE,{"disambiguationData":[TD([[makeQuery(id+"F0.imprint","IMPRINT",EDGE,{"derivedFrom":subQ3}),1.0]])]});}
            var Q18;
            {var subQ3=sQuery(id+"F0.wireOp",EDGE,"E210");Q18=makeQuery(id+"F0.imprint","IMPRINT",FACE,{"disambiguationData":[TD([[makeQuery(id+"F0.imprint","IMPRINT",EDGE,{"derivedFrom":subQ3}),-1.0]])]});}
            var Q19;
            {var subQ5=sQuery(id+"F0.wireOp",EDGE,"E203");Q19=makeQuery(id+"F0.imprint","IMPRINT",FACE,{"disambiguationData":[TD([[makeQuery(id+"F0.imprint","IMPRINT",EDGE,{"derivedFrom":subQ5}),1.0]])]});}
            var Q20;
            {var subQ0=sQuery(id+"F0.wireOp",EDGE,"E152");Q20=makeQuery(id+"F0.imprint","IMPRINT",FACE,{"disambiguationData":[TD([[makeQuery(id+"F0.imprint","IMPRINT",EDGE,{"derivedFrom":subQ0}),1.0]])]});}
            var Q21;
            {var subQ3=sQuery(id+"F0.wireOp",EDGE,"E140");Q21=makeQuery(id+"F0.imprint","IMPRINT",FACE,{"disambiguationData":[TD([[makeQuery(id+"F0.imprint","IMPRINT",EDGE,{"derivedFrom":subQ3}),-1.0]])]});}
            var Q22;
            {var subQ0=sQuery(id+"F0.wireOp",EDGE,"E60");Q22=makeQuery(id+"F0.imprint","IMPRINT",FACE,{"disambiguationData":[TD([[makeQuery(id+"F0.imprint","IMPRINT",EDGE,{"derivedFrom":subQ0}),1.0]])]});}
            var Q23;
            Q23=makeQuery(id+"F0.imprint","IMPRINT",FACE,{"disambiguationData":[TD([[makeQuery(id+"F0.imprint","IMPRINT",EDGE,{"derivedFrom":sQuery(id+"F0.wireOp",EDGE,"E75")}),1.0]])]});
            var Q24;
            {var subQ1=sQuery(id+"F0.wireOp",EDGE,"E116");Q24=makeQuery(id+"F0.imprint","IMPRINT",FACE,{"disambiguationData":[TD([[makeQuery(id+"F0.imprint","IMPRINT",EDGE,{"derivedFrom":subQ1}),1.0]])]});}
            var Q25;
            {var subQ0=sQuery(id+"F0.wireOp",EDGE,"E87");Q25=makeQuery(id+"F0.imprint","IMPRINT",FACE,{"disambiguationData":[TD([[makeQuery(id+"F0.imprint","IMPRINT",EDGE,{"derivedFrom":subQ0}),-1.0]])]});}
            var Q26;
            {var subQ0=sQuery(id+"F0.wireOp",EDGE,"E190");Q26=makeQuery(id+"F0.imprint","IMPRINT",FACE,{"disambiguationData":[TD([[makeQuery(id+"F0.imprint","IMPRINT",EDGE,{"derivedFrom":subQ0}),1.0]])]});}
            var Q27;
            {var subQ0=sQuery(id+"F0.wireOp",EDGE,"E91");Q27=makeQuery(id+"F0.imprint","IMPRINT",FACE,{"disambiguationData":[TD([[makeQuery(id+"F0.imprint","IMPRINT",EDGE,{"derivedFrom":subQ0}),-1.0]])]});}
            var Q28;
            {var subQ0=sQuery(id+"F0.wireOp",EDGE,"E83");Q28=makeQuery(id+"F0.imprint","IMPRINT",FACE,{"disambiguationData":[TD([[makeQuery(id+"F0.imprint","IMPRINT",EDGE,{"derivedFrom":subQ0}),-1.0]])]});}
            var Q29;
            Q29=makeQuery(id+"F0.imprint","IMPRINT",FACE,{"disambiguationData":[TD([[makeQuery(id+"F0.imprint","IMPRINT",EDGE,{"derivedFrom":sQuery(id+"F0.wireOp",EDGE,"E71")}),-1.0]])]});
            var Q30;
            {var subQ0=sQuery(id+"F0.wireOp",EDGE,"E64");Q30=makeQuery(id+"F0.imprint","IMPRINT",FACE,{"disambiguationData":[TD([[makeQuery(id+"F0.imprint","IMPRINT",EDGE,{"derivedFrom":subQ0}),-1.0]])]});}
            var Q31;
            Q31=makeQuery(id+"F0.imprint","IMPRINT",FACE,{"disambiguationData":[TD([[makeQuery(id+"F0.imprint","IMPRINT",EDGE,{"derivedFrom":sQuery(id+"F0.wireOp",EDGE,"E0.bottom")}),1.0]])]});
            var Q32;
            {var subQ0=sQuery(id+"F0.wireOp",EDGE,"E156");Q32=makeQuery(id+"F0.imprint","IMPRINT",FACE,{"disambiguationData":[TD([[makeQuery(id+"F0.imprint","IMPRINT",EDGE,{"derivedFrom":subQ0}),1.0]])]});}
            var Q33;
            Q33=makeQuery(id+"F0.imprint","IMPRINT",FACE,{"disambiguationData":[TD([[makeQuery(id+"F0.imprint","IMPRINT",EDGE,{"derivedFrom":sQuery(id+"F0.wireOp",EDGE,"E159")}),-1.0]])]});
            var Q34;
            {var subQ0=sQuery(id+"F0.wireOp",EDGE,"E202");Q34=makeQuery(id+"F0.imprint","IMPRINT",FACE,{"disambiguationData":[TD([[makeQuery(id+"F0.imprint","IMPRINT",EDGE,{"derivedFrom":subQ0}),1.0]])]});}
            var Q35;
            {var subQ3=sQuery(id+"F0.wireOp",EDGE,"E214");Q35=makeQuery(id+"F0.imprint","IMPRINT",FACE,{"disambiguationData":[TD([[makeQuery(id+"F0.imprint","IMPRINT",EDGE,{"derivedFrom":subQ3}),1.0]])]});}
            var Q36;
            {var subQ3=sQuery(id+"F0.wireOp",EDGE,"E222");Q36=makeQuery(id+"F0.imprint","IMPRINT",FACE,{"disambiguationData":[TD([[makeQuery(id+"F0.imprint","IMPRINT",EDGE,{"derivedFrom":subQ3}),-1.0]])]});}
            var Q37;
            Q37=makeQuery(id+"F0.imprint","IMPRINT",FACE,{"disambiguationData":[TD([[makeQuery(id+"F0.imprint","IMPRINT",EDGE,{"derivedFrom":sQuery(id+"F0.wireOp",EDGE,"E180")}),-1.0]])]});
            var Q38;
            {var subQ4=sQuery(id+"F0.wireOp",EDGE,"E172");Q38=makeQuery(id+"F0.imprint","IMPRINT",FACE,{"disambiguationData":[TD([[makeQuery(id+"F0.imprint","IMPRINT",EDGE,{"derivedFrom":subQ4}),-1.0]])]});}
            var Q39;
            Q39=makeQuery(id+"F0.imprint","IMPRINT",FACE,{"disambiguationData":[TD([[makeQuery(id+"F0.imprint","IMPRINT",EDGE,{"derivedFrom":sQuery(id+"F0.wireOp",EDGE,"E163")}),1.0]])]});
            var Q40;
            Q40=makeQuery(id+"F0.imprint","IMPRINT",FACE,{"disambiguationData":[TD([[makeQuery(id+"F0.imprint","IMPRINT",EDGE,{"derivedFrom":sQuery(id+"F0.wireOp",EDGE,"E79")}),1.0]])]});
            var Q41;
            {var subQ0=sQuery(id+"F0.wireOp",EDGE,"E195");Q41=makeQuery(id+"F0.imprint","IMPRINT",FACE,{"disambiguationData":[TD([[makeQuery(id+"F0.imprint","IMPRINT",EDGE,{"derivedFrom":subQ0}),1.0]])]});}
            var Q42;
            {var subQ4=sQuery(id+"F0.wireOp",EDGE,"E197");Q42=makeQuery(id+"F0.imprint","IMPRINT",FACE,{"disambiguationData":[TD([[makeQuery(id+"F0.imprint","IMPRINT",EDGE,{"derivedFrom":subQ4}),1.0]])]});}
            var Q43;
            {var subQ0=sQuery(id+"F0.wireOp",EDGE,"E198");Q43=makeQuery(id+"F0.imprint","IMPRINT",FACE,{"disambiguationData":[TD([[makeQuery(id+"F0.imprint","IMPRINT",EDGE,{"derivedFrom":subQ0}),-1.0]])]});}
            var Q44;
            {var subQ0=sQuery(id+"F0.wireOp",EDGE,"E167");Q44=makeQuery(id+"F0.imprint","IMPRINT",FACE,{"disambiguationData":[TD([[makeQuery(id+"F0.imprint","IMPRINT",EDGE,{"derivedFrom":subQ0}),-1.0]])]});}
            var Q45;
            Q45=makeQuery(id+"F0.imprint","IMPRINT",FACE,{"disambiguationData":[TD([[makeQuery(id+"F0.imprint","IMPRINT",EDGE,{"derivedFrom":sQuery(id+"F0.wireOp",EDGE,"E223")}),1.0]])]});
            var Q46;
            {var subQ1=sQuery(id+"F0.wireOp",EDGE,"E292");Q46=makeQuery(id+"F0.imprint","IMPRINT",FACE,{"disambiguationData":[TD([[makeQuery(id+"F0.imprint","IMPRINT",EDGE,{"derivedFrom":subQ1}),-1.0]])]});}
            var Q47;
            {var subQ0=sQuery(id+"F0.wireOp",EDGE,"E297");Q47=makeQuery(id+"F0.imprint","IMPRINT",FACE,{"disambiguationData":[TD([[makeQuery(id+"F0.imprint","IMPRINT",EDGE,{"derivedFrom":subQ0}),1.0]])]});}
            var Q48;
            {var subQ0=sQuery(id+"F0.wireOp",EDGE,"E67");Q48=makeQuery(id+"F0.imprint","IMPRINT",FACE,{"disambiguationData":[TD([[makeQuery(id+"F0.imprint","IMPRINT",EDGE,{"derivedFrom":subQ0}),-1.0]])]});}
            var Q49;
            Q49=makeQuery(id+"F0.imprint","IMPRINT",FACE,{"disambiguationData":[TD([[makeQuery(id+"F0.imprint","IMPRINT",EDGE,{"derivedFrom":sQuery(id+"F0.wireOp",EDGE,"E168")}),-1.0]])]});
            var Q50;
            Q50=makeQuery(id+"F0.imprint","IMPRINT",FACE,{"disambiguationData":[TD([[makeQuery(id+"F0.imprint","IMPRINT",EDGE,{"derivedFrom":sQuery(id+"F0.wireOp",EDGE,"E294")}),1.0]])]});
            var Q51;
            Q51=makeQuery(id+"F0.imprint","IMPRINT",FACE,{"disambiguationData":[TD([[makeQuery(id+"F0.imprint","IMPRINT",EDGE,{"derivedFrom":sQuery(id+"F0.wireOp",EDGE,"E176")}),-1.0]])]});
            var Q52;
            {var subQ0=sQuery(id+"F0.wireOp",EDGE,"E216");Q52=makeQuery(id+"F0.imprint","IMPRINT",FACE,{"disambiguationData":[TD([[makeQuery(id+"F0.imprint","IMPRINT",EDGE,{"derivedFrom":subQ0}),-1.0]])]});}
            var Q53;
            Q53=makeQuery(id+"F0.imprint","IMPRINT",FACE,{"disambiguationData":[TD([[makeQuery(id+"F0.imprint","IMPRINT",EDGE,{"derivedFrom":sQuery(id+"F0.wireOp",EDGE,"E184")}),-1.0]])]});
            var Q54;
            {var subQ0=sQuery(id+"F0.wireOp",EDGE,"E302");Q54=makeQuery(id+"F0.imprint","IMPRINT",FACE,{"disambiguationData":[TD([[makeQuery(id+"F0.imprint","IMPRINT",EDGE,{"derivedFrom":subQ0}),-1.0]])]});}
            var Q55;
            {var subQ1=sQuery(id+"F0.wireOp",EDGE,"E258");Q55=makeQuery(id+"F0.imprint","IMPRINT",FACE,{"disambiguationData":[TD([[makeQuery(id+"F0.imprint","IMPRINT",EDGE,{"derivedFrom":subQ1}),1.0]])]});}
            var Q56;
            {var subQ0=sQuery(id+"F0.wireOp",EDGE,"E218");Q56=makeQuery(id+"F0.imprint","IMPRINT",FACE,{"disambiguationData":[TD([[makeQuery(id+"F0.imprint","IMPRINT",EDGE,{"derivedFrom":subQ0}),1.0]])]});}
            var Q57;
            {var subQ0=sQuery(id+"F0.wireOp",EDGE,"E254");Q57=makeQuery(id+"F0.imprint","IMPRINT",FACE,{"disambiguationData":[TD([[makeQuery(id+"F0.imprint","IMPRINT",EDGE,{"derivedFrom":subQ0}),-1.0]])]});}
            extrude(context, id + "F5", {"entities" : qUnion([Q0, Q1, Q2, Q3, Q4, Q5, Q6, Q7, Q8, Q9, Q10, Q11, Q12, Q13, Q14, Q15, Q16, Q17, Q18, Q19, Q20, Q21, Q22, Q23, Q24, Q25, Q26, Q27, Q28, Q29, Q30, Q31, Q32, Q33, Q34, Q35, Q36, Q37, Q38, Q39, Q40, Q41, Q42, Q43, Q44, Q45, Q46, Q47, Q48, Q49, Q50, Q51, Q52, Q53, Q54, Q55, Q56, Q57]), "operationType" : NewBodyOperationType.REMOVE, "oppositeDirection" : true, "depth" : 3 * mm, "offsetDistance" : 25 * mm});
        }
        {
            var Q0;
            Q0=qCreatedBy(makeId("Right.planeOp"),FACE);
            var sketch = newSketch(context, id + "F6", { "sketchPlane" : qUnion([Q0])});
            skPoint(sketch, "E405.0", {"position": v(-282.24, 0) * mm});
            skPoint(sketch, "E406.0", {"position": v(142, 0) * mm});
            skLineSegment(sketch, "E407", {"start": v(-282.24, 0) * mm, "end": v(142, 0) * mm});
            skLineSegment(sketch, "E408", {"start": v(-282.24, 0) * mm, "end": v(-281.78, -7.65) * mm});
            skArc(sketch, "E409", {"start": v(-281.78, -7.65) * mm, "mid": v(-279.63, -12.6) * mm, "end": v(-274.8, -15) * mm});
            skLineSegment(sketch, "E410", {"start": v(-274.8, -15) * mm, "end": v(-124.8, -32) * mm});
            skArc(sketch, "E411", {"start": v(-124.8, -32) * mm, "mid": v(-119.06, -33.48) * mm, "end": v(-113.96, -36.5) * mm});
            skArc(sketch, "E412", {"start": v(-113.96, -36.5) * mm, "mid": v(-107.3, -40.33) * mm, "end": v(-99.8, -42) * mm});
            skLineSegment(sketch, "E413", {"start": v(-99.8, -42) * mm, "end": v(95.2, -55) * mm});
            skLineSegment(sketch, "E414", {"start": v(142, 0) * mm, "end": v(136.71, -23.88) * mm});
            skArc(sketch, "E415", {"start": v(95.2, -55) * mm, "mid": v(121.72, -47.13) * mm, "end": v(136.71, -23.88) * mm});
            skLineSegment(sketch, "E416", {"start": v(95.2, -55) * mm, "end": v(95.2, 0) * mm, "construction": true});
            skLineSegment(sketch, "E417", {"start": v(-99.8, -42) * mm, "end": v(-99.8, 0) * mm, "construction": true});
            skLineSegment(sketch, "E418", {"start": v(-124.8, -32) * mm, "end": v(-124.8, 0) * mm, "construction": true});
            skLineSegment(sketch, "E419", {"start": v(-274.8, -15) * mm, "end": v(-274.8, 0) * mm, "construction": true});
            skSolve(sketch);
        }
        {
            var Q0;
            Q0 = qSketchRegion(id + "F6", true);
            extrude(context, id + "F7", {"entities" : qUnion([Q0]), "endBound" : BoundingType.SYMMETRIC, "depth" : 350 * mm, "offsetDistance" : 25 * mm});
        }
        {
            var Q0;
            Q0=makeQuery(id+"F7.opExtrude","SWEPT_BODY",BODY,{"disambiguationData":[OSD([sQuery(id+"F6.wireOp",EDGE,"E407"),sQuery(id+"F6.wireOp",EDGE,"E408"),sQuery(id+"F6.wireOp",EDGE,"E409"),sQuery(id+"F6.wireOp",EDGE,"E410"),sQuery(id+"F6.wireOp",EDGE,"E411"),sQuery(id+"F6.wireOp",EDGE,"E412"),sQuery(id+"F6.wireOp",EDGE,"E413"),sQuery(id+"F6.wireOp",EDGE,"E414"),sQuery(id+"F6.wireOp",EDGE,"E415")])]});
            var Q1;
            Q1=makeQuery(id+"F3.opExtrude","SWEPT_BODY",BODY,{"disambiguationData":[OSD([sQuery(id+"F2.wireOp",EDGE,"E369.0"),sQuery(id+"F2.wireOp",EDGE,"E370.0"),sQuery(id+"F2.wireOp",EDGE,"E371.0"),sQuery(id+"F2.wireOp",EDGE,"E372.0"),sQuery(id+"F2.wireOp",EDGE,"E373.0"),sQuery(id+"F2.wireOp",EDGE,"E374.0"),sQuery(id+"F2.wireOp",EDGE,"E375.0"),sQuery(id+"F2.wireOp",EDGE,"E376.0"),sQuery(id+"F2.wireOp",EDGE,"E377.0"),sQuery(id+"F2.wireOp",EDGE,"E378.0"),sQuery(id+"F2.wireOp",EDGE,"E379.0"),sQuery(id+"F2.wireOp",EDGE,"E380.0"),sQuery(id+"F2.wireOp",EDGE,"E381.0"),sQuery(id+"F2.wireOp",EDGE,"E382.0"),sQuery(id+"F2.wireOp",EDGE,"E383.0"),sQuery(id+"F2.wireOp",EDGE,"E384.0"),sQuery(id+"F2.wireOp",EDGE,"E385.0"),sQuery(id+"F2.wireOp",EDGE,"E386.0"),sQuery(id+"F2.wireOp",EDGE,"E387.0"),sQuery(id+"F2.wireOp",EDGE,"E388.0"),sQuery(id+"F2.wireOp",EDGE,"E389.0"),sQuery(id+"F2.wireOp",EDGE,"E390.0"),sQuery(id+"F2.wireOp",EDGE,"E391.0"),sQuery(id+"F2.wireOp",EDGE,"E392.0"),sQuery(id+"F2.wireOp",EDGE,"E393.0"),sQuery(id+"F2.wireOp",EDGE,"E394.0"),sQuery(id+"F2.wireOp",EDGE,"E395.0"),sQuery(id+"F2.wireOp",EDGE,"E396.0"),sQuery(id+"F2.wireOp",EDGE,"E397.0"),sQuery(id+"F2.wireOp",EDGE,"E398.0"),sQuery(id+"F2.wireOp",EDGE,"E399.0"),sQuery(id+"F2.wireOp",EDGE,"E400.0"),sQuery(id+"F2.wireOp",EDGE,"E401.0"),sQuery(id+"F2.wireOp",EDGE,"E402.0"),sQuery(id+"F2.wireOp",EDGE,"E403.0"),sQuery(id+"F2.wireOp",EDGE,"E404.0")])]});
            var Q2;
            Q2=makeQuery(id+"F3.opExtrude","SWEPT_BODY",BODY,{"disambiguationData":[OSD([sQuery(id+"F2.wireOp",EDGE,"E369.0"),sQuery(id+"F2.wireOp",EDGE,"E370.0"),sQuery(id+"F2.wireOp",EDGE,"E371.0"),sQuery(id+"F2.wireOp",EDGE,"E372.0"),sQuery(id+"F2.wireOp",EDGE,"E373.0"),sQuery(id+"F2.wireOp",EDGE,"E374.0"),sQuery(id+"F2.wireOp",EDGE,"E375.0"),sQuery(id+"F2.wireOp",EDGE,"E376.0"),sQuery(id+"F2.wireOp",EDGE,"E377.0"),sQuery(id+"F2.wireOp",EDGE,"E378.0"),sQuery(id+"F2.wireOp",EDGE,"E379.0"),sQuery(id+"F2.wireOp",EDGE,"E380.0"),sQuery(id+"F2.wireOp",EDGE,"E381.0"),sQuery(id+"F2.wireOp",EDGE,"E382.0"),sQuery(id+"F2.wireOp",EDGE,"E383.0"),sQuery(id+"F2.wireOp",EDGE,"E384.0"),sQuery(id+"F2.wireOp",EDGE,"E385.0"),sQuery(id+"F2.wireOp",EDGE,"E386.0"),sQuery(id+"F2.wireOp",EDGE,"E387.0"),sQuery(id+"F2.wireOp",EDGE,"E388.0"),sQuery(id+"F2.wireOp",EDGE,"E389.0"),sQuery(id+"F2.wireOp",EDGE,"E390.0"),sQuery(id+"F2.wireOp",EDGE,"E391.0"),sQuery(id+"F2.wireOp",EDGE,"E392.0"),sQuery(id+"F2.wireOp",EDGE,"E393.0"),sQuery(id+"F2.wireOp",EDGE,"E394.0"),sQuery(id+"F2.wireOp",EDGE,"E395.0"),sQuery(id+"F2.wireOp",EDGE,"E396.0"),sQuery(id+"F2.wireOp",EDGE,"E397.0"),sQuery(id+"F2.wireOp",EDGE,"E398.0"),sQuery(id+"F2.wireOp",EDGE,"E399.0"),sQuery(id+"F2.wireOp",EDGE,"E400.0"),sQuery(id+"F2.wireOp",EDGE,"E401.0"),sQuery(id+"F2.wireOp",EDGE,"E402.0"),sQuery(id+"F2.wireOp",EDGE,"E403.0"),sQuery(id+"F2.wireOp",EDGE,"E404.0")])]});
            booleanBodies(context, id + "F8", {"operationType" : BooleanOperationType.INTERSECTION, "tools" : qUnion([Q0, Q1]), "targets" : qUnion([Q2])});
        }
        {
            var Q0;
            Q0=makeQuery(id+"F8.opBoolean","INTERSECT",EDGE,{"derivedFrom":[makeQuery(id+"F3.opExtrude","SWEPT_FACE",FACE,{"disambiguationData":[OSD([sQuery(id+"F2.wireOp",EDGE,"E393.0"),sQuery(id+"F2.wireOp",EDGE,"E394.0")])]}),makeQuery(id+"F7.opExtrude","SWEPT_FACE",FACE,{"disambiguationData":[OSD([sQuery(id+"F6.wireOp",EDGE,"E413")])]})]});
            var Q1;
            Q1=makeQuery(id+"F8.opBoolean","INTERSECT",EDGE,{"derivedFrom":[makeQuery(id+"F3.opExtrude","SWEPT_FACE",FACE,{"disambiguationData":[OSD([sQuery(id+"F2.wireOp",EDGE,"E392.0")])]}),makeQuery(id+"F7.opExtrude","SWEPT_FACE",FACE,{"disambiguationData":[OSD([sQuery(id+"F6.wireOp",EDGE,"E413")])]})]});
            var Q2;
            Q2=makeQuery(id+"F8.opBoolean","INTERSECT",EDGE,{"derivedFrom":[makeQuery(id+"F3.opExtrude","SWEPT_FACE",FACE,{"disambiguationData":[OSD([sQuery(id+"F2.wireOp",EDGE,"E391.0")])]}),makeQuery(id+"F7.opExtrude","SWEPT_FACE",FACE,{"disambiguationData":[OSD([sQuery(id+"F6.wireOp",EDGE,"E413")])]})]});
            var Q3;
            Q3=makeQuery(id+"F8.opBoolean","INTERSECT",EDGE,{"derivedFrom":[makeQuery(id+"F3.opExtrude","SWEPT_FACE",FACE,{"disambiguationData":[OSD([sQuery(id+"F2.wireOp",EDGE,"E390.0")])]}),makeQuery(id+"F7.opExtrude","SWEPT_FACE",FACE,{"disambiguationData":[OSD([sQuery(id+"F6.wireOp",EDGE,"E413")])]})]});
            var Q4;
            Q4=makeQuery(id+"F8.opBoolean","INTERSECT",EDGE,{"derivedFrom":[makeQuery(id+"F3.opExtrude","SWEPT_FACE",FACE,{"disambiguationData":[OSD([sQuery(id+"F2.wireOp",EDGE,"E389.0")])]}),makeQuery(id+"F7.opExtrude","SWEPT_FACE",FACE,{"disambiguationData":[OSD([sQuery(id+"F6.wireOp",EDGE,"E413")])]})]});
            var Q5;
            Q5=makeQuery(id+"F8.opBoolean","INTERSECT",EDGE,{"derivedFrom":[makeQuery(id+"F3.opExtrude","SWEPT_FACE",FACE,{"disambiguationData":[OSD([sQuery(id+"F2.wireOp",EDGE,"E388.0")])]}),makeQuery(id+"F7.opExtrude","SWEPT_FACE",FACE,{"disambiguationData":[OSD([sQuery(id+"F6.wireOp",EDGE,"E413")])]})]});
            var Q6;
            Q6=makeQuery(id+"F8.opBoolean","INTERSECT",EDGE,{"derivedFrom":[makeQuery(id+"F3.opExtrude","SWEPT_FACE",FACE,{"disambiguationData":[OSD([sQuery(id+"F2.wireOp",EDGE,"E387.0")])]}),makeQuery(id+"F7.opExtrude","SWEPT_FACE",FACE,{"disambiguationData":[OSD([sQuery(id+"F6.wireOp",EDGE,"E413")])]})]});
            var Q7;
            Q7=makeQuery(id+"F8.opBoolean","INTERSECT",EDGE,{"derivedFrom":[makeQuery(id+"F3.opExtrude","SWEPT_FACE",FACE,{"disambiguationData":[OSD([sQuery(id+"F2.wireOp",EDGE,"E387.0")])]}),makeQuery(id+"F7.opExtrude","SWEPT_FACE",FACE,{"disambiguationData":[OSD([sQuery(id+"F6.wireOp",EDGE,"E415")])]})]});
            var Q8;
            Q8=makeQuery(id+"F8.opBoolean","INTERSECT",EDGE,{"derivedFrom":[makeQuery(id+"F3.opExtrude","SWEPT_FACE",FACE,{"disambiguationData":[OSD([sQuery(id+"F2.wireOp",EDGE,"E386.0")])]}),makeQuery(id+"F7.opExtrude","SWEPT_FACE",FACE,{"disambiguationData":[OSD([sQuery(id+"F6.wireOp",EDGE,"E415")])]})]});
            var Q9;
            Q9=makeQuery(id+"F8.opBoolean","INTERSECT",EDGE,{"derivedFrom":[makeQuery(id+"F3.opExtrude","SWEPT_FACE",FACE,{"disambiguationData":[OSD([sQuery(id+"F2.wireOp",EDGE,"E386.0")])]}),makeQuery(id+"F7.opExtrude","SWEPT_FACE",FACE,{"disambiguationData":[OSD([sQuery(id+"F6.wireOp",EDGE,"E414")])]})]});
            var Q10;
            Q10=makeQuery(id+"F3.opExtrude","SWEPT_EDGE",EDGE,{"disambiguationData":[OSD([sQuery(id+"F2.wireOp",EDGE,"E386.0"),sQuery(id+"F2.wireOp",EDGE,"E404.0")])]});
            var Q11;
            Q11=makeQuery(id+"F3.opExtrude","SWEPT_EDGE",EDGE,{"disambiguationData":[OSD([sQuery(id+"F2.wireOp",EDGE,"E385.0"),sQuery(id+"F2.wireOp",EDGE,"E404.0")])]});
            var Q12;
            Q12=makeQuery(id+"F8.opBoolean","INTERSECT",EDGE,{"derivedFrom":[makeQuery(id+"F3.opExtrude","SWEPT_FACE",FACE,{"disambiguationData":[OSD([sQuery(id+"F2.wireOp",EDGE,"E385.0")])]}),makeQuery(id+"F7.opExtrude","SWEPT_FACE",FACE,{"disambiguationData":[OSD([sQuery(id+"F6.wireOp",EDGE,"E414")])]})]});
            var Q13;
            Q13=makeQuery(id+"F8.opBoolean","INTERSECT",EDGE,{"derivedFrom":[makeQuery(id+"F3.opExtrude","SWEPT_FACE",FACE,{"disambiguationData":[OSD([sQuery(id+"F2.wireOp",EDGE,"E385.0")])]}),makeQuery(id+"F7.opExtrude","SWEPT_FACE",FACE,{"disambiguationData":[OSD([sQuery(id+"F6.wireOp",EDGE,"E415")])]})]});
            var Q14;
            Q14=makeQuery(id+"F8.opBoolean","INTERSECT",EDGE,{"derivedFrom":[makeQuery(id+"F3.opExtrude","SWEPT_FACE",FACE,{"disambiguationData":[OSD([sQuery(id+"F2.wireOp",EDGE,"E384.0")])]}),makeQuery(id+"F7.opExtrude","SWEPT_FACE",FACE,{"disambiguationData":[OSD([sQuery(id+"F6.wireOp",EDGE,"E415")])]})]});
            var Q15;
            Q15=makeQuery(id+"F8.opBoolean","INTERSECT",EDGE,{"derivedFrom":[makeQuery(id+"F3.opExtrude","SWEPT_FACE",FACE,{"disambiguationData":[OSD([sQuery(id+"F2.wireOp",EDGE,"E384.0")])]}),makeQuery(id+"F7.opExtrude","SWEPT_FACE",FACE,{"disambiguationData":[OSD([sQuery(id+"F6.wireOp",EDGE,"E413")])]})]});
            var Q16;
            Q16=makeQuery(id+"F8.opBoolean","INTERSECT",EDGE,{"derivedFrom":[makeQuery(id+"F3.opExtrude","SWEPT_FACE",FACE,{"disambiguationData":[OSD([sQuery(id+"F2.wireOp",EDGE,"E383.0")])]}),makeQuery(id+"F7.opExtrude","SWEPT_FACE",FACE,{"disambiguationData":[OSD([sQuery(id+"F6.wireOp",EDGE,"E413")])]})]});
            var Q17;
            Q17=makeQuery(id+"F8.opBoolean","INTERSECT",EDGE,{"derivedFrom":[makeQuery(id+"F3.opExtrude","SWEPT_FACE",FACE,{"disambiguationData":[OSD([sQuery(id+"F2.wireOp",EDGE,"E382.0")])]}),makeQuery(id+"F7.opExtrude","SWEPT_FACE",FACE,{"disambiguationData":[OSD([sQuery(id+"F6.wireOp",EDGE,"E413")])]})]});
            var Q18;
            Q18=makeQuery(id+"F8.opBoolean","INTERSECT",EDGE,{"derivedFrom":[makeQuery(id+"F3.opExtrude","SWEPT_FACE",FACE,{"disambiguationData":[OSD([sQuery(id+"F2.wireOp",EDGE,"E381.0")])]}),makeQuery(id+"F7.opExtrude","SWEPT_FACE",FACE,{"disambiguationData":[OSD([sQuery(id+"F6.wireOp",EDGE,"E413")])]})]});
            var Q19;
            Q19=makeQuery(id+"F8.opBoolean","INTERSECT",EDGE,{"derivedFrom":[makeQuery(id+"F3.opExtrude","SWEPT_FACE",FACE,{"disambiguationData":[OSD([sQuery(id+"F2.wireOp",EDGE,"E380.0")])]}),makeQuery(id+"F7.opExtrude","SWEPT_FACE",FACE,{"disambiguationData":[OSD([sQuery(id+"F6.wireOp",EDGE,"E413")])]})]});
            var Q20;
            Q20=makeQuery(id+"F8.opBoolean","INTERSECT",EDGE,{"derivedFrom":[makeQuery(id+"F3.opExtrude","SWEPT_FACE",FACE,{"disambiguationData":[OSD([sQuery(id+"F2.wireOp",EDGE,"E378.0"),sQuery(id+"F2.wireOp",EDGE,"E379.0")])]}),makeQuery(id+"F7.opExtrude","SWEPT_FACE",FACE,{"disambiguationData":[OSD([sQuery(id+"F6.wireOp",EDGE,"E413")])]})]});
            var Q21;
            Q21=makeQuery(id+"F8.opBoolean","INTERSECT",EDGE,{"derivedFrom":[makeQuery(id+"F3.opExtrude","SWEPT_FACE",FACE,{"disambiguationData":[OSD([sQuery(id+"F2.wireOp",EDGE,"E378.0"),sQuery(id+"F2.wireOp",EDGE,"E379.0")])]}),makeQuery(id+"F7.opExtrude","SWEPT_FACE",FACE,{"disambiguationData":[OSD([sQuery(id+"F6.wireOp",EDGE,"E412")])]})]});
            var Q22;
            Q22=makeQuery(id+"F8.opBoolean","INTERSECT",EDGE,{"derivedFrom":[makeQuery(id+"F3.opExtrude","SWEPT_FACE",FACE,{"disambiguationData":[OSD([sQuery(id+"F2.wireOp",EDGE,"E377.0")])]}),makeQuery(id+"F7.opExtrude","SWEPT_FACE",FACE,{"disambiguationData":[OSD([sQuery(id+"F6.wireOp",EDGE,"E412")])]})]});
            var Q23;
            Q23=makeQuery(id+"F8.opBoolean","INTERSECT",EDGE,{"derivedFrom":[makeQuery(id+"F3.opExtrude","SWEPT_FACE",FACE,{"disambiguationData":[OSD([sQuery(id+"F2.wireOp",EDGE,"E377.0")])]}),makeQuery(id+"F7.opExtrude","SWEPT_FACE",FACE,{"disambiguationData":[OSD([sQuery(id+"F6.wireOp",EDGE,"E411")])]})]});
            var Q24;
            Q24=makeQuery(id+"F8.opBoolean","INTERSECT",EDGE,{"derivedFrom":[makeQuery(id+"F3.opExtrude","SWEPT_FACE",FACE,{"disambiguationData":[OSD([sQuery(id+"F2.wireOp",EDGE,"E375.0"),sQuery(id+"F2.wireOp",EDGE,"E376.0")])]}),makeQuery(id+"F7.opExtrude","SWEPT_FACE",FACE,{"disambiguationData":[OSD([sQuery(id+"F6.wireOp",EDGE,"E410")])]})]});
            var Q25;
            Q25=makeQuery(id+"F8.opBoolean","INTERSECT",EDGE,{"derivedFrom":[makeQuery(id+"F3.opExtrude","SWEPT_FACE",FACE,{"disambiguationData":[OSD([sQuery(id+"F2.wireOp",EDGE,"E374.0")])]}),makeQuery(id+"F7.opExtrude","SWEPT_FACE",FACE,{"disambiguationData":[OSD([sQuery(id+"F6.wireOp",EDGE,"E410")])]})]});
            var Q26;
            Q26=makeQuery(id+"F8.opBoolean","INTERSECT",EDGE,{"derivedFrom":[makeQuery(id+"F3.opExtrude","SWEPT_FACE",FACE,{"disambiguationData":[OSD([sQuery(id+"F2.wireOp",EDGE,"E373.0")])]}),makeQuery(id+"F7.opExtrude","SWEPT_FACE",FACE,{"disambiguationData":[OSD([sQuery(id+"F6.wireOp",EDGE,"E410")])]})]});
            var Q27;
            Q27=makeQuery(id+"F8.opBoolean","INTERSECT",EDGE,{"derivedFrom":[makeQuery(id+"F3.opExtrude","SWEPT_FACE",FACE,{"disambiguationData":[OSD([sQuery(id+"F2.wireOp",EDGE,"E372.0")])]}),makeQuery(id+"F7.opExtrude","SWEPT_FACE",FACE,{"disambiguationData":[OSD([sQuery(id+"F6.wireOp",EDGE,"E410")])]})]});
            var Q28;
            Q28=makeQuery(id+"F8.opBoolean","INTERSECT",EDGE,{"derivedFrom":[makeQuery(id+"F3.opExtrude","SWEPT_FACE",FACE,{"disambiguationData":[OSD([sQuery(id+"F2.wireOp",EDGE,"E371.0")])]}),makeQuery(id+"F7.opExtrude","SWEPT_FACE",FACE,{"disambiguationData":[OSD([sQuery(id+"F6.wireOp",EDGE,"E410")])]})]});
            var Q29;
            Q29=makeQuery(id+"F8.opBoolean","INTERSECT",EDGE,{"derivedFrom":[makeQuery(id+"F3.opExtrude","SWEPT_FACE",FACE,{"disambiguationData":[OSD([sQuery(id+"F2.wireOp",EDGE,"E401.0")])]}),makeQuery(id+"F7.opExtrude","SWEPT_FACE",FACE,{"disambiguationData":[OSD([sQuery(id+"F6.wireOp",EDGE,"E410")])]})]});
            var Q30;
            Q30=makeQuery(id+"F8.opBoolean","INTERSECT",EDGE,{"derivedFrom":[makeQuery(id+"F3.opExtrude","SWEPT_FACE",FACE,{"disambiguationData":[OSD([sQuery(id+"F2.wireOp",EDGE,"E400.0")])]}),makeQuery(id+"F7.opExtrude","SWEPT_FACE",FACE,{"disambiguationData":[OSD([sQuery(id+"F6.wireOp",EDGE,"E410")])]})]});
            var Q31;
            Q31=makeQuery(id+"F8.opBoolean","INTERSECT",EDGE,{"derivedFrom":[makeQuery(id+"F3.opExtrude","SWEPT_FACE",FACE,{"disambiguationData":[OSD([sQuery(id+"F2.wireOp",EDGE,"E399.0")])]}),makeQuery(id+"F7.opExtrude","SWEPT_FACE",FACE,{"disambiguationData":[OSD([sQuery(id+"F6.wireOp",EDGE,"E410")])]})]});
            var Q32;
            Q32=makeQuery(id+"F8.opBoolean","INTERSECT",EDGE,{"derivedFrom":[makeQuery(id+"F3.opExtrude","SWEPT_FACE",FACE,{"disambiguationData":[OSD([sQuery(id+"F2.wireOp",EDGE,"E395.0")])]}),makeQuery(id+"F7.opExtrude","SWEPT_FACE",FACE,{"disambiguationData":[OSD([sQuery(id+"F6.wireOp",EDGE,"E412")])]})]});
            var Q33;
            Q33=makeQuery(id+"F8.opBoolean","INTERSECT",EDGE,{"derivedFrom":[makeQuery(id+"F3.opExtrude","SWEPT_FACE",FACE,{"disambiguationData":[OSD([sQuery(id+"F2.wireOp",EDGE,"E395.0")])]}),makeQuery(id+"F7.opExtrude","SWEPT_FACE",FACE,{"disambiguationData":[OSD([sQuery(id+"F6.wireOp",EDGE,"E411")])]})]});
            var Q34;
            Q34=makeQuery(id+"F8.opBoolean","INTERSECT",EDGE,{"derivedFrom":[makeQuery(id+"F3.opExtrude","SWEPT_FACE",FACE,{"disambiguationData":[OSD([sQuery(id+"F2.wireOp",EDGE,"E398.0")])]}),makeQuery(id+"F7.opExtrude","SWEPT_FACE",FACE,{"disambiguationData":[OSD([sQuery(id+"F6.wireOp",EDGE,"E410")])]})]});
            var Q35;
            Q35=makeQuery(id+"F8.opBoolean","INTERSECT",EDGE,{"derivedFrom":[makeQuery(id+"F3.opExtrude","SWEPT_FACE",FACE,{"disambiguationData":[OSD([sQuery(id+"F2.wireOp",EDGE,"E393.0"),sQuery(id+"F2.wireOp",EDGE,"E394.0")])]}),makeQuery(id+"F7.opExtrude","SWEPT_FACE",FACE,{"disambiguationData":[OSD([sQuery(id+"F6.wireOp",EDGE,"E412")])]})]});
            var Q36;
            Q36=makeQuery(id+"F8.opBoolean","INTERSECT",EDGE,{"derivedFrom":[makeQuery(id+"F3.opExtrude","SWEPT_FACE",FACE,{"disambiguationData":[OSD([sQuery(id+"F2.wireOp",EDGE,"E396.0"),sQuery(id+"F2.wireOp",EDGE,"E397.0")])]}),makeQuery(id+"F7.opExtrude","SWEPT_FACE",FACE,{"disambiguationData":[OSD([sQuery(id+"F6.wireOp",EDGE,"E410")])]})]});
            var Q37;
            Q37=makeQuery(id+"F8.opBoolean","INTERSECT",EDGE,{"derivedFrom":[makeQuery(id+"F3.opExtrude","SWEPT_FACE",FACE,{"disambiguationData":[OSD([sQuery(id+"F2.wireOp",EDGE,"E401.0")])]}),makeQuery(id+"F7.opExtrude","SWEPT_FACE",FACE,{"disambiguationData":[OSD([sQuery(id+"F6.wireOp",EDGE,"E409")])]})]});
            var Q38;
            Q38=makeQuery(id+"F8.opBoolean","INTERSECT",EDGE,{"derivedFrom":[makeQuery(id+"F3.opExtrude","SWEPT_FACE",FACE,{"disambiguationData":[OSD([sQuery(id+"F2.wireOp",EDGE,"E371.0")])]}),makeQuery(id+"F7.opExtrude","SWEPT_FACE",FACE,{"disambiguationData":[OSD([sQuery(id+"F6.wireOp",EDGE,"E409")])]})]});
            var Q39;
            Q39=makeQuery(id+"F8.opBoolean","INTERSECT",EDGE,{"derivedFrom":[makeQuery(id+"F3.opExtrude","SWEPT_FACE",FACE,{"disambiguationData":[OSD([sQuery(id+"F2.wireOp",EDGE,"E402.0")])]}),makeQuery(id+"F7.opExtrude","SWEPT_FACE",FACE,{"disambiguationData":[OSD([sQuery(id+"F6.wireOp",EDGE,"E409")])]})]});
            var Q40;
            Q40=makeQuery(id+"F8.opBoolean","INTERSECT",EDGE,{"derivedFrom":[makeQuery(id+"F3.opExtrude","SWEPT_FACE",FACE,{"disambiguationData":[OSD([sQuery(id+"F2.wireOp",EDGE,"E370.0")])]}),makeQuery(id+"F7.opExtrude","SWEPT_FACE",FACE,{"disambiguationData":[OSD([sQuery(id+"F6.wireOp",EDGE,"E409")])]})]});
            fillet(context, id + "F9", {"entities" : qUnion([Q0, Q1, Q2, Q3, Q4, Q5, Q6, Q7, Q8, Q9, Q10, Q11, Q12, Q13, Q14, Q15, Q16, Q17, Q18, Q19, Q20, Q21, Q22, Q23, Q24, Q25, Q26, Q27, Q28, Q29, Q30, Q31, Q32, Q33, Q34, Q35, Q36, Q37, Q38, Q39, Q40]), "radius" : 8 * mm, "tangentPropagation" : true, "allowEdgeOverflow" : false});
        }
    });
